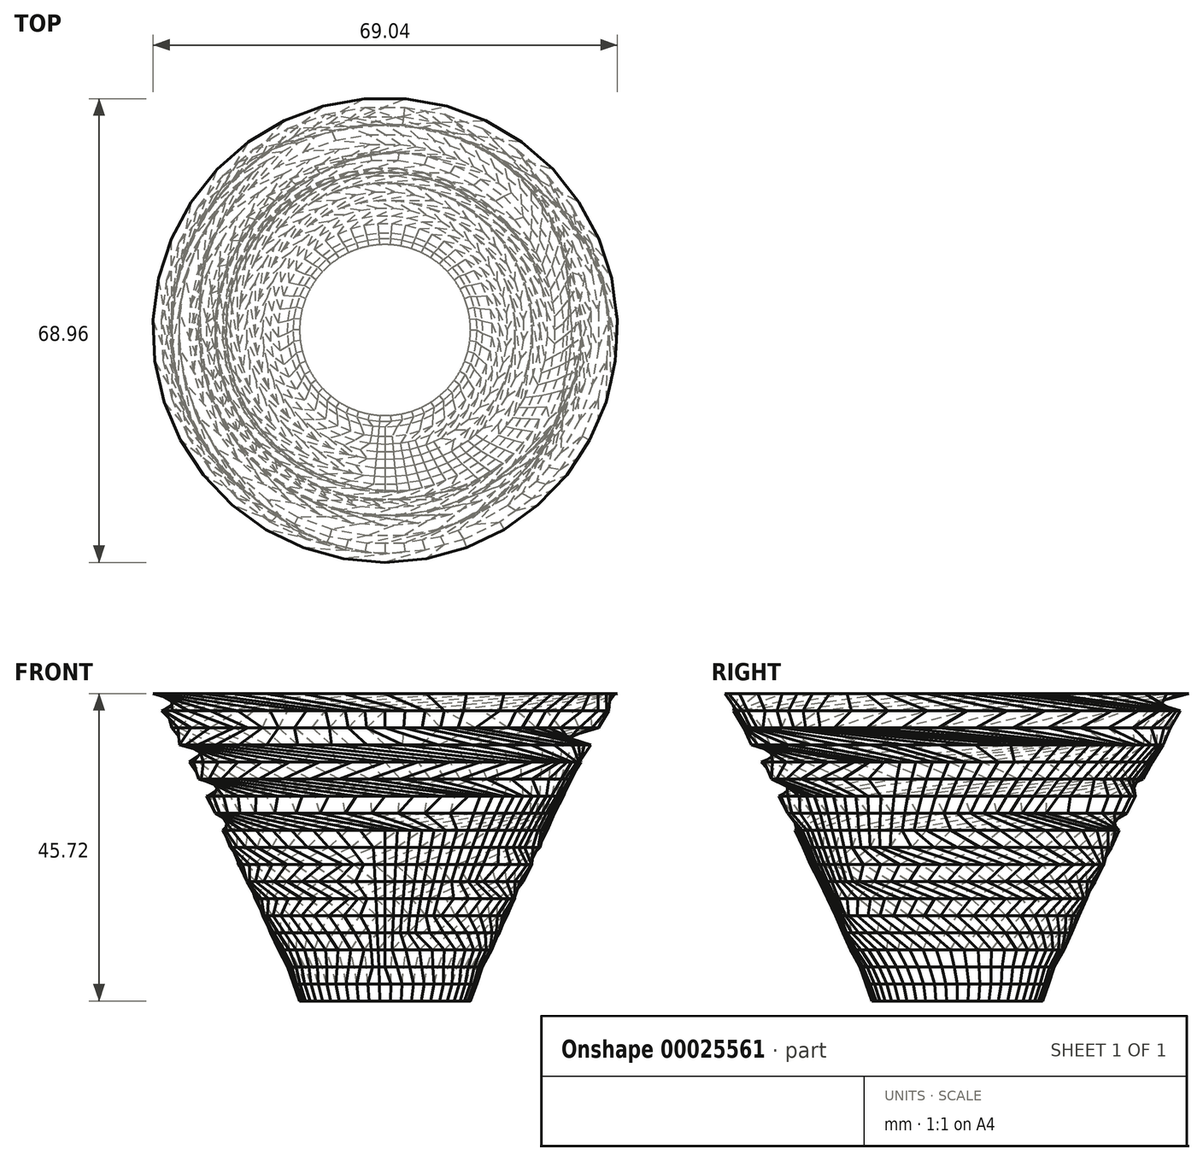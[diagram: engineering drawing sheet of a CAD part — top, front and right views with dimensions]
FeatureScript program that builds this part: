
annotation { "Feature Type Name" : "Feature", "Feature Type Description" : "" }
export const myFeature = defineFeature(function(context is Context, id is Id, definition is map)
    precondition{}
    {
        {
            var Q0;
            Q0=qCreatedBy(makeId("Top.planeOp"),FACE);
            var sketch = newSketch(context, id + "F0", { "sketchPlane" : qUnion([Q0])});
            skCircle(sketch, "E0", {"center": v(0, 0) * mm, "radius": 12.7 * mm});
            skSolve(sketch);
        }
        {
            var Q0;
            Q0=qCreatedBy(makeId("Top.planeOp"),FACE);
            cPlane(context, id + "F1", {"entities" : qUnion([Q0]), "cplaneType" : CPlaneType.OFFSET, "offset" : 2.54 * mm, "width" : 152.4 * mm, "height" : 152.4 * mm});
        }
        {
            var Q0;
            Q0=qCreatedBy(id+"F1.planeOp",FACE);
            var sketch = newSketch(context, id + "F2", { "sketchPlane" : qUnion([Q0])});
            skPoint(sketch, "E1.0", {"position": v(0, 0) * mm});
            skCircle(sketch, "E2.cCircle", {"center": v(0, 0) * mm, "radius": 13.6 * mm, "construction": true});
            skLineSegment(sketch, "E2.0", {"start": v(-0.86, 13.6) * mm, "end": v(0.86, 13.6) * mm});
            skLineSegment(sketch, "E2.1", {"start": v(0.86, 13.6) * mm, "end": v(2.55, 13.38) * mm});
            skLineSegment(sketch, "E2.2", {"start": v(2.55, 13.38) * mm, "end": v(4.2, 12.95) * mm});
            skLineSegment(sketch, "E2.3", {"start": v(4.2, 12.95) * mm, "end": v(5.8, 12.33) * mm});
            skLineSegment(sketch, "E2.4", {"start": v(5.8, 12.33) * mm, "end": v(7.3, 11.5) * mm});
            skLineSegment(sketch, "E2.5", {"start": v(7.3, 11.5) * mm, "end": v(8.68, 10.5) * mm});
            skLineSegment(sketch, "E2.6", {"start": v(8.68, 10.5) * mm, "end": v(9.93, 9.32) * mm});
            skLineSegment(sketch, "E2.7", {"start": v(9.93, 9.32) * mm, "end": v(11.02, 8) * mm});
            skLineSegment(sketch, "E2.8", {"start": v(11.02, 8) * mm, "end": v(11.94, 6.56) * mm});
            skLineSegment(sketch, "E2.9", {"start": v(11.94, 6.56) * mm, "end": v(12.66, 5.01) * mm});
            skLineSegment(sketch, "E2.10", {"start": v(12.66, 5.01) * mm, "end": v(13.2, 3.39) * mm});
            skLineSegment(sketch, "E2.11", {"start": v(13.2, 3.39) * mm, "end": v(13.51, 1.7) * mm});
            skLineSegment(sketch, "E2.12", {"start": v(13.51, 1.7) * mm, "end": v(13.62, 0) * mm});
            skLineSegment(sketch, "E2.13", {"start": v(13.62, 0) * mm, "end": v(13.51, -1.7) * mm});
            skLineSegment(sketch, "E2.14", {"start": v(13.51, -1.7) * mm, "end": v(13.2, -3.39) * mm});
            skLineSegment(sketch, "E2.15", {"start": v(13.2, -3.39) * mm, "end": v(12.66, -5.01) * mm});
            skLineSegment(sketch, "E2.16", {"start": v(12.66, -5.01) * mm, "end": v(11.94, -6.56) * mm});
            skLineSegment(sketch, "E2.17", {"start": v(11.94, -6.56) * mm, "end": v(11.02, -8) * mm});
            skLineSegment(sketch, "E2.18", {"start": v(11.02, -8) * mm, "end": v(9.93, -9.32) * mm});
            skLineSegment(sketch, "E2.19", {"start": v(9.93, -9.32) * mm, "end": v(8.68, -10.5) * mm});
            skLineSegment(sketch, "E2.20", {"start": v(8.68, -10.5) * mm, "end": v(7.3, -11.5) * mm});
            skLineSegment(sketch, "E2.21", {"start": v(7.3, -11.5) * mm, "end": v(5.8, -12.33) * mm});
            skLineSegment(sketch, "E2.22", {"start": v(5.8, -12.33) * mm, "end": v(4.2, -12.95) * mm});
            skLineSegment(sketch, "E2.23", {"start": v(4.2, -12.95) * mm, "end": v(2.55, -13.38) * mm});
            skLineSegment(sketch, "E2.24", {"start": v(2.55, -13.38) * mm, "end": v(0.86, -13.6) * mm});
            skLineSegment(sketch, "E2.25", {"start": v(0.86, -13.6) * mm, "end": v(-0.86, -13.6) * mm});
            skLineSegment(sketch, "E2.26", {"start": v(-0.86, -13.6) * mm, "end": v(-2.55, -13.38) * mm});
            skLineSegment(sketch, "E2.27", {"start": v(-2.55, -13.38) * mm, "end": v(-4.2, -12.95) * mm});
            skLineSegment(sketch, "E2.28", {"start": v(-4.2, -12.95) * mm, "end": v(-5.8, -12.33) * mm});
            skLineSegment(sketch, "E2.29", {"start": v(-5.8, -12.33) * mm, "end": v(-7.3, -11.5) * mm});
            skLineSegment(sketch, "E2.30", {"start": v(-7.3, -11.5) * mm, "end": v(-8.68, -10.5) * mm});
            skLineSegment(sketch, "E2.31", {"start": v(-8.68, -10.5) * mm, "end": v(-9.93, -9.32) * mm});
            skLineSegment(sketch, "E2.32", {"start": v(-9.93, -9.32) * mm, "end": v(-11.02, -8) * mm});
            skLineSegment(sketch, "E2.33", {"start": v(-11.02, -8) * mm, "end": v(-11.94, -6.56) * mm});
            skLineSegment(sketch, "E2.34", {"start": v(-11.94, -6.56) * mm, "end": v(-12.66, -5.01) * mm});
            skLineSegment(sketch, "E2.35", {"start": v(-12.66, -5.01) * mm, "end": v(-13.2, -3.39) * mm});
            skLineSegment(sketch, "E2.36", {"start": v(-13.2, -3.39) * mm, "end": v(-13.51, -1.7) * mm});
            skLineSegment(sketch, "E2.37", {"start": v(-13.51, -1.7) * mm, "end": v(-13.62, 0) * mm});
            skLineSegment(sketch, "E2.38", {"start": v(-13.62, 0) * mm, "end": v(-13.51, 1.7) * mm});
            skLineSegment(sketch, "E2.39", {"start": v(-13.51, 1.7) * mm, "end": v(-13.2, 3.39) * mm});
            skLineSegment(sketch, "E2.40", {"start": v(-13.2, 3.39) * mm, "end": v(-12.66, 5.01) * mm});
            skLineSegment(sketch, "E2.41", {"start": v(-12.66, 5.01) * mm, "end": v(-11.94, 6.56) * mm});
            skLineSegment(sketch, "E2.42", {"start": v(-11.94, 6.56) * mm, "end": v(-11.02, 8) * mm});
            skLineSegment(sketch, "E2.43", {"start": v(-11.02, 8) * mm, "end": v(-9.93, 9.32) * mm});
            skLineSegment(sketch, "E2.44", {"start": v(-9.93, 9.32) * mm, "end": v(-8.68, 10.5) * mm});
            skLineSegment(sketch, "E2.45", {"start": v(-8.68, 10.5) * mm, "end": v(-7.3, 11.5) * mm});
            skLineSegment(sketch, "E2.46", {"start": v(-7.3, 11.5) * mm, "end": v(-5.8, 12.33) * mm});
            skLineSegment(sketch, "E2.47", {"start": v(-5.8, 12.33) * mm, "end": v(-4.2, 12.95) * mm});
            skLineSegment(sketch, "E2.48", {"start": v(-4.2, 12.95) * mm, "end": v(-2.55, 13.38) * mm});
            skLineSegment(sketch, "E2.49", {"start": v(-2.55, 13.38) * mm, "end": v(-0.86, 13.6) * mm});
            skPoint(sketch, "E2.0.midPoint", {"position": v(0, 13.6) * mm});
            skSolve(sketch);
        }
        {
            var Q0;
            Q0=makeQuery(id+"F0.imprint","IMPRINT",FACE,{"disambiguationData":[TD([[makeQuery(id+"F0.imprint","IMPRINT",EDGE,{"derivedFrom":sQuery(id+"F0.wireOp",EDGE,"E0")}),1.0]])]});
            var Q1;
            Q1=makeQuery(id+"F2.imprint","IMPRINT",FACE,{"disambiguationData":[TD([[makeQuery(id+"F2.imprint","IMPRINT",EDGE,{"derivedFrom":sQuery(id+"F2.wireOp",EDGE,"E2.0")}),-1.0]])]});
            loft(context, id + "F3", {"sheetProfilesArray" : [{ "sheetProfileEntities" : qUnion([Q0]) }, { "sheetProfileEntities" : qUnion([Q1]) }]});
        }
        {
            var Q0;
            Q0=qCreatedBy(id+"F1.planeOp",FACE);
            cPlane(context, id + "F4", {"entities" : qUnion([Q0]), "cplaneType" : CPlaneType.OFFSET, "offset" : 2.54 * mm, "width" : 152.4 * mm, "height" : 152.4 * mm});
        }
        {
            var Q0;
            Q0=qCreatedBy(id+"F4.planeOp",FACE);
            var sketch = newSketch(context, id + "F5", { "sketchPlane" : qUnion([Q0])});
            skCircle(sketch, "E3.cCircle", {"center": v(0, 0) * mm, "radius": 14.44 * mm, "construction": true});
            skLineSegment(sketch, "E3.0", {"start": v(-0.93, 14.44) * mm, "end": v(0.93, 14.44) * mm});
            skLineSegment(sketch, "E3.1", {"start": v(0.93, 14.44) * mm, "end": v(2.77, 14.2) * mm});
            skLineSegment(sketch, "E3.2", {"start": v(2.77, 14.2) * mm, "end": v(4.56, 13.74) * mm});
            skLineSegment(sketch, "E3.3", {"start": v(4.56, 13.74) * mm, "end": v(6.28, 13.04) * mm});
            skLineSegment(sketch, "E3.4", {"start": v(6.28, 13.04) * mm, "end": v(7.9, 12.13) * mm});
            skLineSegment(sketch, "E3.5", {"start": v(7.9, 12.13) * mm, "end": v(9.38, 11.02) * mm});
            skLineSegment(sketch, "E3.6", {"start": v(9.38, 11.02) * mm, "end": v(10.71, 9.73) * mm});
            skLineSegment(sketch, "E3.7", {"start": v(10.71, 9.73) * mm, "end": v(11.87, 8.28) * mm});
            skLineSegment(sketch, "E3.8", {"start": v(11.87, 8.28) * mm, "end": v(12.83, 6.7) * mm});
            skLineSegment(sketch, "E3.9", {"start": v(12.83, 6.7) * mm, "end": v(13.58, 5) * mm});
            skLineSegment(sketch, "E3.10", {"start": v(13.58, 5) * mm, "end": v(14.11, 3.22) * mm});
            skLineSegment(sketch, "E3.11", {"start": v(14.11, 3.22) * mm, "end": v(14.4, 1.39) * mm});
            skLineSegment(sketch, "E3.12", {"start": v(14.4, 1.39) * mm, "end": v(14.47, -0.46) * mm});
            skLineSegment(sketch, "E3.13", {"start": v(14.47, -0.46) * mm, "end": v(14.29, -2.31) * mm});
            skLineSegment(sketch, "E3.14", {"start": v(14.29, -2.31) * mm, "end": v(13.88, -4.12) * mm});
            skLineSegment(sketch, "E3.15", {"start": v(13.88, -4.12) * mm, "end": v(13.24, -5.86) * mm});
            skLineSegment(sketch, "E3.16", {"start": v(13.24, -5.86) * mm, "end": v(12.38, -7.5) * mm});
            skLineSegment(sketch, "E3.17", {"start": v(12.38, -7.5) * mm, "end": v(11.32, -9.02) * mm});
            skLineSegment(sketch, "E3.18", {"start": v(11.32, -9.02) * mm, "end": v(10.07, -10.4) * mm});
            skLineSegment(sketch, "E3.19", {"start": v(10.07, -10.4) * mm, "end": v(8.66, -11.6) * mm});
            skLineSegment(sketch, "E3.20", {"start": v(8.66, -11.6) * mm, "end": v(7.1, -12.61) * mm});
            skLineSegment(sketch, "E3.21", {"start": v(7.1, -12.61) * mm, "end": v(5.43, -13.42) * mm});
            skLineSegment(sketch, "E3.22", {"start": v(5.43, -13.42) * mm, "end": v(3.67, -14) * mm});
            skLineSegment(sketch, "E3.23", {"start": v(3.67, -14) * mm, "end": v(1.85, -14.36) * mm});
            skLineSegment(sketch, "E3.24", {"start": v(1.85, -14.36) * mm, "end": v(0, -14.47) * mm});
            skLineSegment(sketch, "E3.25", {"start": v(0, -14.47) * mm, "end": v(-1.85, -14.36) * mm});
            skLineSegment(sketch, "E3.26", {"start": v(-1.85, -14.36) * mm, "end": v(-3.67, -14) * mm});
            skLineSegment(sketch, "E3.27", {"start": v(-3.67, -14) * mm, "end": v(-5.43, -13.42) * mm});
            skLineSegment(sketch, "E3.28", {"start": v(-5.43, -13.42) * mm, "end": v(-7.1, -12.61) * mm});
            skLineSegment(sketch, "E3.29", {"start": v(-7.1, -12.61) * mm, "end": v(-8.66, -11.6) * mm});
            skLineSegment(sketch, "E3.30", {"start": v(-8.66, -11.6) * mm, "end": v(-10.07, -10.4) * mm});
            skLineSegment(sketch, "E3.31", {"start": v(-10.07, -10.4) * mm, "end": v(-11.32, -9.02) * mm});
            skLineSegment(sketch, "E3.32", {"start": v(-11.32, -9.02) * mm, "end": v(-12.38, -7.5) * mm});
            skLineSegment(sketch, "E3.33", {"start": v(-12.38, -7.5) * mm, "end": v(-13.24, -5.86) * mm});
            skLineSegment(sketch, "E3.34", {"start": v(-13.24, -5.86) * mm, "end": v(-13.88, -4.12) * mm});
            skLineSegment(sketch, "E3.35", {"start": v(-13.88, -4.12) * mm, "end": v(-14.29, -2.31) * mm});
            skLineSegment(sketch, "E3.36", {"start": v(-14.29, -2.31) * mm, "end": v(-14.47, -0.46) * mm});
            skLineSegment(sketch, "E3.37", {"start": v(-14.47, -0.46) * mm, "end": v(-14.4, 1.39) * mm});
            skLineSegment(sketch, "E3.38", {"start": v(-14.4, 1.39) * mm, "end": v(-14.11, 3.22) * mm});
            skLineSegment(sketch, "E3.39", {"start": v(-14.11, 3.22) * mm, "end": v(-13.58, 5) * mm});
            skLineSegment(sketch, "E3.40", {"start": v(-13.58, 5) * mm, "end": v(-12.83, 6.7) * mm});
            skLineSegment(sketch, "E3.41", {"start": v(-12.83, 6.7) * mm, "end": v(-11.87, 8.28) * mm});
            skLineSegment(sketch, "E3.42", {"start": v(-11.87, 8.28) * mm, "end": v(-10.71, 9.73) * mm});
            skLineSegment(sketch, "E3.43", {"start": v(-10.71, 9.73) * mm, "end": v(-9.38, 11.02) * mm});
            skLineSegment(sketch, "E3.44", {"start": v(-9.38, 11.02) * mm, "end": v(-7.9, 12.13) * mm});
            skLineSegment(sketch, "E3.45", {"start": v(-7.9, 12.13) * mm, "end": v(-6.28, 13.04) * mm});
            skLineSegment(sketch, "E3.46", {"start": v(-6.28, 13.04) * mm, "end": v(-4.56, 13.74) * mm});
            skLineSegment(sketch, "E3.47", {"start": v(-4.56, 13.74) * mm, "end": v(-2.77, 14.2) * mm});
            skLineSegment(sketch, "E3.48", {"start": v(-2.77, 14.2) * mm, "end": v(-0.93, 14.44) * mm});
            skPoint(sketch, "E3.0.midPoint", {"position": v(0, 14.44) * mm});
            skSolve(sketch);
        }
        {
            var Q1;
            Q1=makeQuery(id+"F3.opLoft","CAP_FACE",FACE,{"disambiguationData":[OSD([makeQuery(id+"F2.imprint","IMPRINT",FACE,{"disambiguationData":[TD([[makeQuery(id+"F2.imprint","IMPRINT",EDGE,{"derivedFrom":sQuery(id+"F2.wireOp",EDGE,"E2.0")}),-1.0]])]})])],"isStart":true});
            var Q2;
            Q2=makeQuery(id+"F5.imprint","IMPRINT",FACE,{"disambiguationData":[TD([[makeQuery(id+"F5.imprint","IMPRINT",EDGE,{"derivedFrom":sQuery(id+"F5.wireOp",EDGE,"E3.0")}),-1.0]])]});
            loft(context, id + "F6", {"operationType" : NewBodyOperationType.ADD, "sheetProfilesArray" : [{ "sheetProfileEntities" : qUnion([Q1]) }, { "sheetProfileEntities" : qUnion([Q2]) }]});
        }
        {
            var Q0;
            Q0=qCreatedBy(id+"F4.planeOp",FACE);
            cPlane(context, id + "F7", {"entities" : qUnion([Q0]), "cplaneType" : CPlaneType.OFFSET, "offset" : 2.54 * mm, "width" : 152.4 * mm, "height" : 152.4 * mm});
        }
        {
            var Q0;
            Q0=qCreatedBy(id+"F7.planeOp",FACE);
            var sketch = newSketch(context, id + "F8", { "sketchPlane" : qUnion([Q0])});
            skCircle(sketch, "E4.cCircle", {"center": v(0, 0) * mm, "radius": 15.86 * mm, "construction": true});
            skLineSegment(sketch, "E4.0", {"start": v(-1.04, 15.86) * mm, "end": v(1.04, 15.86) * mm});
            skLineSegment(sketch, "E4.1", {"start": v(1.04, 15.86) * mm, "end": v(3.1, 15.59) * mm});
            skLineSegment(sketch, "E4.2", {"start": v(3.1, 15.59) * mm, "end": v(5.1, 15.05) * mm});
            skLineSegment(sketch, "E4.3", {"start": v(5.1, 15.05) * mm, "end": v(7.03, 14.26) * mm});
            skLineSegment(sketch, "E4.4", {"start": v(7.03, 14.26) * mm, "end": v(8.83, 13.22) * mm});
            skLineSegment(sketch, "E4.5", {"start": v(8.83, 13.22) * mm, "end": v(10.48, 11.95) * mm});
            skLineSegment(sketch, "E4.6", {"start": v(10.48, 11.95) * mm, "end": v(11.95, 10.48) * mm});
            skLineSegment(sketch, "E4.7", {"start": v(11.95, 10.48) * mm, "end": v(13.22, 8.83) * mm});
            skLineSegment(sketch, "E4.8", {"start": v(13.22, 8.83) * mm, "end": v(14.26, 7.03) * mm});
            skLineSegment(sketch, "E4.9", {"start": v(14.26, 7.03) * mm, "end": v(15.05, 5.1) * mm});
            skLineSegment(sketch, "E4.10", {"start": v(15.05, 5.1) * mm, "end": v(15.59, 3.1) * mm});
            skLineSegment(sketch, "E4.11", {"start": v(15.59, 3.1) * mm, "end": v(15.86, 1.04) * mm});
            skLineSegment(sketch, "E4.12", {"start": v(15.86, 1.04) * mm, "end": v(15.86, -1.04) * mm});
            skLineSegment(sketch, "E4.13", {"start": v(15.86, -1.04) * mm, "end": v(15.59, -3.1) * mm});
            skLineSegment(sketch, "E4.14", {"start": v(15.59, -3.1) * mm, "end": v(15.05, -5.1) * mm});
            skLineSegment(sketch, "E4.15", {"start": v(15.05, -5.1) * mm, "end": v(14.26, -7.03) * mm});
            skLineSegment(sketch, "E4.16", {"start": v(14.26, -7.03) * mm, "end": v(13.22, -8.83) * mm});
            skLineSegment(sketch, "E4.17", {"start": v(13.22, -8.83) * mm, "end": v(11.95, -10.48) * mm});
            skLineSegment(sketch, "E4.18", {"start": v(11.95, -10.48) * mm, "end": v(10.48, -11.95) * mm});
            skLineSegment(sketch, "E4.19", {"start": v(10.48, -11.95) * mm, "end": v(8.83, -13.22) * mm});
            skLineSegment(sketch, "E4.20", {"start": v(8.83, -13.22) * mm, "end": v(7.03, -14.26) * mm});
            skLineSegment(sketch, "E4.21", {"start": v(7.03, -14.26) * mm, "end": v(5.1, -15.05) * mm});
            skLineSegment(sketch, "E4.22", {"start": v(5.1, -15.05) * mm, "end": v(3.1, -15.59) * mm});
            skLineSegment(sketch, "E4.23", {"start": v(3.1, -15.59) * mm, "end": v(1.04, -15.86) * mm});
            skLineSegment(sketch, "E4.24", {"start": v(1.04, -15.86) * mm, "end": v(-1.04, -15.86) * mm});
            skLineSegment(sketch, "E4.25", {"start": v(-1.04, -15.86) * mm, "end": v(-3.1, -15.59) * mm});
            skLineSegment(sketch, "E4.26", {"start": v(-3.1, -15.59) * mm, "end": v(-5.1, -15.05) * mm});
            skLineSegment(sketch, "E4.27", {"start": v(-5.1, -15.05) * mm, "end": v(-7.03, -14.26) * mm});
            skLineSegment(sketch, "E4.28", {"start": v(-7.03, -14.26) * mm, "end": v(-8.83, -13.22) * mm});
            skLineSegment(sketch, "E4.29", {"start": v(-8.83, -13.22) * mm, "end": v(-10.48, -11.95) * mm});
            skLineSegment(sketch, "E4.30", {"start": v(-10.48, -11.95) * mm, "end": v(-11.95, -10.48) * mm});
            skLineSegment(sketch, "E4.31", {"start": v(-11.95, -10.48) * mm, "end": v(-13.22, -8.83) * mm});
            skLineSegment(sketch, "E4.32", {"start": v(-13.22, -8.83) * mm, "end": v(-14.26, -7.03) * mm});
            skLineSegment(sketch, "E4.33", {"start": v(-14.26, -7.03) * mm, "end": v(-15.05, -5.1) * mm});
            skLineSegment(sketch, "E4.34", {"start": v(-15.05, -5.1) * mm, "end": v(-15.59, -3.1) * mm});
            skLineSegment(sketch, "E4.35", {"start": v(-15.59, -3.1) * mm, "end": v(-15.86, -1.04) * mm});
            skLineSegment(sketch, "E4.36", {"start": v(-15.86, -1.04) * mm, "end": v(-15.86, 1.04) * mm});
            skLineSegment(sketch, "E4.37", {"start": v(-15.86, 1.04) * mm, "end": v(-15.59, 3.1) * mm});
            skLineSegment(sketch, "E4.38", {"start": v(-15.59, 3.1) * mm, "end": v(-15.05, 5.1) * mm});
            skLineSegment(sketch, "E4.39", {"start": v(-15.05, 5.1) * mm, "end": v(-14.26, 7.03) * mm});
            skLineSegment(sketch, "E4.40", {"start": v(-14.26, 7.03) * mm, "end": v(-13.22, 8.83) * mm});
            skLineSegment(sketch, "E4.41", {"start": v(-13.22, 8.83) * mm, "end": v(-11.95, 10.48) * mm});
            skLineSegment(sketch, "E4.42", {"start": v(-11.95, 10.48) * mm, "end": v(-10.48, 11.95) * mm});
            skLineSegment(sketch, "E4.43", {"start": v(-10.48, 11.95) * mm, "end": v(-8.83, 13.22) * mm});
            skLineSegment(sketch, "E4.44", {"start": v(-8.83, 13.22) * mm, "end": v(-7.03, 14.26) * mm});
            skLineSegment(sketch, "E4.45", {"start": v(-7.03, 14.26) * mm, "end": v(-5.1, 15.05) * mm});
            skLineSegment(sketch, "E4.46", {"start": v(-5.1, 15.05) * mm, "end": v(-3.1, 15.59) * mm});
            skLineSegment(sketch, "E4.47", {"start": v(-3.1, 15.59) * mm, "end": v(-1.04, 15.86) * mm});
            skPoint(sketch, "E4.0.midPoint", {"position": v(0, 15.86) * mm});
            skSolve(sketch);
        }
        {
            var Q1;
            Q1=makeQuery(id+"F6.opLoft","CAP_FACE",FACE,{"disambiguationData":[OSD([makeQuery(id+"F5.imprint","IMPRINT",FACE,{"disambiguationData":[TD([[makeQuery(id+"F5.imprint","IMPRINT",EDGE,{"derivedFrom":sQuery(id+"F5.wireOp",EDGE,"E3.0")}),-1.0]])]})])],"isStart":true});
            var Q2;
            Q2=makeQuery(id+"F8.imprint","IMPRINT",FACE,{"disambiguationData":[TD([[makeQuery(id+"F8.imprint","IMPRINT",EDGE,{"derivedFrom":sQuery(id+"F8.wireOp",EDGE,"E4.0")}),-1.0]])]});
            loft(context, id + "F9", {"operationType" : NewBodyOperationType.ADD, "sheetProfilesArray" : [{ "sheetProfileEntities" : qUnion([Q1]) }, { "sheetProfileEntities" : qUnion([Q2]) }]});
        }
        {
            var Q0;
            Q0=qCreatedBy(id+"F7.planeOp",FACE);
            cPlane(context, id + "F10", {"entities" : qUnion([Q0]), "cplaneType" : CPlaneType.OFFSET, "offset" : 2.54 * mm, "width" : 152.4 * mm, "height" : 152.4 * mm});
        }
        {
            var Q0;
            Q0=qCreatedBy(id+"F10.planeOp",FACE);
            var sketch = newSketch(context, id + "F11", { "sketchPlane" : qUnion([Q0])});
            skCircle(sketch, "E5.cCircle", {"center": v(0, 0) * mm, "radius": 17 * mm, "construction": true});
            skLineSegment(sketch, "E5.0", {"start": v(-1.14, 17) * mm, "end": v(1.14, 17) * mm});
            skLineSegment(sketch, "E5.1", {"start": v(1.14, 17) * mm, "end": v(3.4, 16.7) * mm});
            skLineSegment(sketch, "E5.2", {"start": v(3.4, 16.7) * mm, "end": v(5.59, 16.09) * mm});
            skLineSegment(sketch, "E5.3", {"start": v(5.59, 16.09) * mm, "end": v(7.68, 15.2) * mm});
            skLineSegment(sketch, "E5.4", {"start": v(7.68, 15.2) * mm, "end": v(9.64, 14.04) * mm});
            skLineSegment(sketch, "E5.5", {"start": v(9.64, 14.04) * mm, "end": v(11.42, 12.63) * mm});
            skLineSegment(sketch, "E5.6", {"start": v(11.42, 12.63) * mm, "end": v(13, 11) * mm});
            skLineSegment(sketch, "E5.7", {"start": v(13, 11) * mm, "end": v(14.36, 9.16) * mm});
            skLineSegment(sketch, "E5.8", {"start": v(14.36, 9.16) * mm, "end": v(15.45, 7.17) * mm});
            skLineSegment(sketch, "E5.9", {"start": v(15.45, 7.17) * mm, "end": v(16.27, 5.05) * mm});
            skLineSegment(sketch, "E5.10", {"start": v(16.27, 5.05) * mm, "end": v(16.8, 2.83) * mm});
            skLineSegment(sketch, "E5.11", {"start": v(16.8, 2.83) * mm, "end": v(17.02, 0.57) * mm});
            skLineSegment(sketch, "E5.12", {"start": v(17.02, 0.57) * mm, "end": v(16.95, -1.7) * mm});
            skLineSegment(sketch, "E5.13", {"start": v(16.95, -1.7) * mm, "end": v(16.57, -3.95) * mm});
            skLineSegment(sketch, "E5.14", {"start": v(16.57, -3.95) * mm, "end": v(15.9, -6.12) * mm});
            skLineSegment(sketch, "E5.15", {"start": v(15.9, -6.12) * mm, "end": v(14.94, -8.18) * mm});
            skLineSegment(sketch, "E5.16", {"start": v(14.94, -8.18) * mm, "end": v(13.71, -10.1) * mm});
            skLineSegment(sketch, "E5.17", {"start": v(13.71, -10.1) * mm, "end": v(12.24, -11.84) * mm});
            skLineSegment(sketch, "E5.18", {"start": v(12.24, -11.84) * mm, "end": v(10.56, -13.37) * mm});
            skLineSegment(sketch, "E5.19", {"start": v(10.56, -13.37) * mm, "end": v(8.68, -14.65) * mm});
            skLineSegment(sketch, "E5.20", {"start": v(8.68, -14.65) * mm, "end": v(6.65, -15.68) * mm});
            skLineSegment(sketch, "E5.21", {"start": v(6.65, -15.68) * mm, "end": v(4.5, -16.43) * mm});
            skLineSegment(sketch, "E5.22", {"start": v(4.5, -16.43) * mm, "end": v(2.27, -16.88) * mm});
            skLineSegment(sketch, "E5.23", {"start": v(2.27, -16.88) * mm, "end": v(0, -17.03) * mm});
            skLineSegment(sketch, "E5.24", {"start": v(0, -17.03) * mm, "end": v(-2.27, -16.88) * mm});
            skLineSegment(sketch, "E5.25", {"start": v(-2.27, -16.88) * mm, "end": v(-4.5, -16.43) * mm});
            skLineSegment(sketch, "E5.26", {"start": v(-4.5, -16.43) * mm, "end": v(-6.65, -15.68) * mm});
            skLineSegment(sketch, "E5.27", {"start": v(-6.65, -15.68) * mm, "end": v(-8.68, -14.65) * mm});
            skLineSegment(sketch, "E5.28", {"start": v(-8.68, -14.65) * mm, "end": v(-10.56, -13.37) * mm});
            skLineSegment(sketch, "E5.29", {"start": v(-10.56, -13.37) * mm, "end": v(-12.24, -11.84) * mm});
            skLineSegment(sketch, "E5.30", {"start": v(-12.24, -11.84) * mm, "end": v(-13.71, -10.1) * mm});
            skLineSegment(sketch, "E5.31", {"start": v(-13.71, -10.1) * mm, "end": v(-14.94, -8.18) * mm});
            skLineSegment(sketch, "E5.32", {"start": v(-14.94, -8.18) * mm, "end": v(-15.9, -6.12) * mm});
            skLineSegment(sketch, "E5.33", {"start": v(-15.9, -6.12) * mm, "end": v(-16.57, -3.95) * mm});
            skLineSegment(sketch, "E5.34", {"start": v(-16.57, -3.95) * mm, "end": v(-16.95, -1.7) * mm});
            skLineSegment(sketch, "E5.35", {"start": v(-16.95, -1.7) * mm, "end": v(-17.02, 0.57) * mm});
            skLineSegment(sketch, "E5.36", {"start": v(-17.02, 0.57) * mm, "end": v(-16.8, 2.83) * mm});
            skLineSegment(sketch, "E5.37", {"start": v(-16.8, 2.83) * mm, "end": v(-16.27, 5.05) * mm});
            skLineSegment(sketch, "E5.38", {"start": v(-16.27, 5.05) * mm, "end": v(-15.45, 7.17) * mm});
            skLineSegment(sketch, "E5.39", {"start": v(-15.45, 7.17) * mm, "end": v(-14.36, 9.16) * mm});
            skLineSegment(sketch, "E5.40", {"start": v(-14.36, 9.16) * mm, "end": v(-13, 11) * mm});
            skLineSegment(sketch, "E5.41", {"start": v(-13, 11) * mm, "end": v(-11.42, 12.63) * mm});
            skLineSegment(sketch, "E5.42", {"start": v(-11.42, 12.63) * mm, "end": v(-9.64, 14.04) * mm});
            skLineSegment(sketch, "E5.43", {"start": v(-9.64, 14.04) * mm, "end": v(-7.68, 15.2) * mm});
            skLineSegment(sketch, "E5.44", {"start": v(-7.68, 15.2) * mm, "end": v(-5.59, 16.09) * mm});
            skLineSegment(sketch, "E5.45", {"start": v(-5.59, 16.09) * mm, "end": v(-3.4, 16.7) * mm});
            skLineSegment(sketch, "E5.46", {"start": v(-3.4, 16.7) * mm, "end": v(-1.14, 17) * mm});
            skPoint(sketch, "E5.0.midPoint", {"position": v(0, 17) * mm});
            skSolve(sketch);
        }
        {
            var Q1;
            Q1=makeQuery(id+"F9.opLoft","CAP_FACE",FACE,{"disambiguationData":[OSD([makeQuery(id+"F8.imprint","IMPRINT",FACE,{"disambiguationData":[TD([[makeQuery(id+"F8.imprint","IMPRINT",EDGE,{"derivedFrom":sQuery(id+"F8.wireOp",EDGE,"E4.0")}),-1.0]])]})])],"isStart":true});
            var Q2;
            Q2=makeQuery(id+"F11.imprint","IMPRINT",FACE,{"disambiguationData":[TD([[makeQuery(id+"F11.imprint","IMPRINT",EDGE,{"derivedFrom":sQuery(id+"F11.wireOp",EDGE,"E5.0")}),-1.0]])]});
            loft(context, id + "F12", {"operationType" : NewBodyOperationType.ADD, "sheetProfilesArray" : [{ "sheetProfileEntities" : qUnion([Q1]) }, { "sheetProfileEntities" : qUnion([Q2]) }]});
        }
        {
            var Q0;
            Q0=qCreatedBy(id+"F10.planeOp",FACE);
            cPlane(context, id + "F13", {"entities" : qUnion([Q0]), "cplaneType" : CPlaneType.OFFSET, "offset" : 2.54 * mm, "width" : 152.4 * mm, "height" : 152.4 * mm});
        }
        {
            var Q0;
            Q0=qCreatedBy(id+"F13.planeOp",FACE);
            var sketch = newSketch(context, id + "F14", { "sketchPlane" : qUnion([Q0])});
            skCircle(sketch, "E6.cCircle", {"center": v(0, 0) * mm, "radius": 18.13 * mm, "construction": true});
            skLineSegment(sketch, "E6.0", {"start": v(-1.24, 18.13) * mm, "end": v(1.24, 18.13) * mm});
            skLineSegment(sketch, "E6.1", {"start": v(1.24, 18.13) * mm, "end": v(3.7, 17.79) * mm});
            skLineSegment(sketch, "E6.2", {"start": v(3.7, 17.79) * mm, "end": v(6.08, 17.12) * mm});
            skLineSegment(sketch, "E6.3", {"start": v(6.08, 17.12) * mm, "end": v(8.36, 16.13) * mm});
            skLineSegment(sketch, "E6.4", {"start": v(8.36, 16.13) * mm, "end": v(10.48, 14.84) * mm});
            skLineSegment(sketch, "E6.5", {"start": v(10.48, 14.84) * mm, "end": v(12.4, 13.28) * mm});
            skLineSegment(sketch, "E6.6", {"start": v(12.4, 13.28) * mm, "end": v(14.1, 11.47) * mm});
            skLineSegment(sketch, "E6.7", {"start": v(14.1, 11.47) * mm, "end": v(15.52, 9.44) * mm});
            skLineSegment(sketch, "E6.8", {"start": v(15.52, 9.44) * mm, "end": v(16.66, 7.24) * mm});
            skLineSegment(sketch, "E6.9", {"start": v(16.66, 7.24) * mm, "end": v(17.5, 4.9) * mm});
            skLineSegment(sketch, "E6.10", {"start": v(17.5, 4.9) * mm, "end": v(18, 2.47) * mm});
            skLineSegment(sketch, "E6.11", {"start": v(18, 2.47) * mm, "end": v(18.17, 0) * mm});
            skLineSegment(sketch, "E6.12", {"start": v(18.17, 0) * mm, "end": v(18, -2.47) * mm});
            skLineSegment(sketch, "E6.13", {"start": v(18, -2.47) * mm, "end": v(17.5, -4.9) * mm});
            skLineSegment(sketch, "E6.14", {"start": v(17.5, -4.9) * mm, "end": v(16.66, -7.24) * mm});
            skLineSegment(sketch, "E6.15", {"start": v(16.66, -7.24) * mm, "end": v(15.52, -9.44) * mm});
            skLineSegment(sketch, "E6.16", {"start": v(15.52, -9.44) * mm, "end": v(14.1, -11.47) * mm});
            skLineSegment(sketch, "E6.17", {"start": v(14.1, -11.47) * mm, "end": v(12.4, -13.28) * mm});
            skLineSegment(sketch, "E6.18", {"start": v(12.4, -13.28) * mm, "end": v(10.48, -14.84) * mm});
            skLineSegment(sketch, "E6.19", {"start": v(10.48, -14.84) * mm, "end": v(8.36, -16.13) * mm});
            skLineSegment(sketch, "E6.20", {"start": v(8.36, -16.13) * mm, "end": v(6.08, -17.12) * mm});
            skLineSegment(sketch, "E6.21", {"start": v(6.08, -17.12) * mm, "end": v(3.7, -17.79) * mm});
            skLineSegment(sketch, "E6.22", {"start": v(3.7, -17.79) * mm, "end": v(1.24, -18.13) * mm});
            skLineSegment(sketch, "E6.23", {"start": v(1.24, -18.13) * mm, "end": v(-1.24, -18.13) * mm});
            skLineSegment(sketch, "E6.24", {"start": v(-1.24, -18.13) * mm, "end": v(-3.7, -17.79) * mm});
            skLineSegment(sketch, "E6.25", {"start": v(-3.7, -17.79) * mm, "end": v(-6.08, -17.12) * mm});
            skLineSegment(sketch, "E6.26", {"start": v(-6.08, -17.12) * mm, "end": v(-8.36, -16.13) * mm});
            skLineSegment(sketch, "E6.27", {"start": v(-8.36, -16.13) * mm, "end": v(-10.48, -14.84) * mm});
            skLineSegment(sketch, "E6.28", {"start": v(-10.48, -14.84) * mm, "end": v(-12.4, -13.28) * mm});
            skLineSegment(sketch, "E6.29", {"start": v(-12.4, -13.28) * mm, "end": v(-14.1, -11.47) * mm});
            skLineSegment(sketch, "E6.30", {"start": v(-14.1, -11.47) * mm, "end": v(-15.52, -9.44) * mm});
            skLineSegment(sketch, "E6.31", {"start": v(-15.52, -9.44) * mm, "end": v(-16.66, -7.24) * mm});
            skLineSegment(sketch, "E6.32", {"start": v(-16.66, -7.24) * mm, "end": v(-17.5, -4.9) * mm});
            skLineSegment(sketch, "E6.33", {"start": v(-17.5, -4.9) * mm, "end": v(-18, -2.47) * mm});
            skLineSegment(sketch, "E6.34", {"start": v(-18, -2.47) * mm, "end": v(-18.17, 0) * mm});
            skLineSegment(sketch, "E6.35", {"start": v(-18.17, 0) * mm, "end": v(-18, 2.47) * mm});
            skLineSegment(sketch, "E6.36", {"start": v(-18, 2.47) * mm, "end": v(-17.5, 4.9) * mm});
            skLineSegment(sketch, "E6.37", {"start": v(-17.5, 4.9) * mm, "end": v(-16.66, 7.24) * mm});
            skLineSegment(sketch, "E6.38", {"start": v(-16.66, 7.24) * mm, "end": v(-15.52, 9.44) * mm});
            skLineSegment(sketch, "E6.39", {"start": v(-15.52, 9.44) * mm, "end": v(-14.1, 11.47) * mm});
            skLineSegment(sketch, "E6.40", {"start": v(-14.1, 11.47) * mm, "end": v(-12.4, 13.28) * mm});
            skLineSegment(sketch, "E6.41", {"start": v(-12.4, 13.28) * mm, "end": v(-10.48, 14.84) * mm});
            skLineSegment(sketch, "E6.42", {"start": v(-10.48, 14.84) * mm, "end": v(-8.36, 16.13) * mm});
            skLineSegment(sketch, "E6.43", {"start": v(-8.36, 16.13) * mm, "end": v(-6.08, 17.12) * mm});
            skLineSegment(sketch, "E6.44", {"start": v(-6.08, 17.12) * mm, "end": v(-3.7, 17.79) * mm});
            skLineSegment(sketch, "E6.45", {"start": v(-3.7, 17.79) * mm, "end": v(-1.24, 18.13) * mm});
            skPoint(sketch, "E6.0.midPoint", {"position": v(0, 18.13) * mm});
            skSolve(sketch);
        }
        {
            var Q1;
            Q1=makeQuery(id+"F12.opLoft","CAP_FACE",FACE,{"disambiguationData":[OSD([makeQuery(id+"F11.imprint","IMPRINT",FACE,{"disambiguationData":[TD([[makeQuery(id+"F11.imprint","IMPRINT",EDGE,{"derivedFrom":sQuery(id+"F11.wireOp",EDGE,"E5.0")}),-1.0]])]})])],"isStart":true});
            var Q2;
            Q2=makeQuery(id+"F14.imprint","IMPRINT",FACE,{"disambiguationData":[TD([[makeQuery(id+"F14.imprint","IMPRINT",EDGE,{"derivedFrom":sQuery(id+"F14.wireOp",EDGE,"E6.0")}),-1.0]])]});
            loft(context, id + "F15", {"operationType" : NewBodyOperationType.ADD, "sheetProfilesArray" : [{ "sheetProfileEntities" : qUnion([Q1]) }, { "sheetProfileEntities" : qUnion([Q2]) }]});
        }
        {
            var Q0;
            Q0=qCreatedBy(id+"F13.planeOp",FACE);
            cPlane(context, id + "F16", {"entities" : qUnion([Q0]), "cplaneType" : CPlaneType.OFFSET, "offset" : 2.54 * mm, "width" : 152.4 * mm, "height" : 152.4 * mm});
        }
        {
            var Q0;
            Q0=qCreatedBy(id+"F16.planeOp",FACE);
            var sketch = newSketch(context, id + "F17", { "sketchPlane" : qUnion([Q0])});
            skCircle(sketch, "E7.cCircle", {"center": v(0, 0) * mm, "radius": 19.26 * mm, "construction": true});
            skLineSegment(sketch, "E7.0", {"start": v(-1.35, 19.26) * mm, "end": v(1.35, 19.26) * mm});
            skLineSegment(sketch, "E7.1", {"start": v(1.35, 19.26) * mm, "end": v(4.01, 18.88) * mm});
            skLineSegment(sketch, "E7.2", {"start": v(4.01, 18.88) * mm, "end": v(6.6, 18.14) * mm});
            skLineSegment(sketch, "E7.3", {"start": v(6.6, 18.14) * mm, "end": v(9.06, 17.05) * mm});
            skLineSegment(sketch, "E7.4", {"start": v(9.06, 17.05) * mm, "end": v(11.35, 15.62) * mm});
            skLineSegment(sketch, "E7.5", {"start": v(11.35, 15.62) * mm, "end": v(13.41, 13.89) * mm});
            skLineSegment(sketch, "E7.6", {"start": v(13.41, 13.89) * mm, "end": v(15.21, 11.89) * mm});
            skLineSegment(sketch, "E7.7", {"start": v(15.21, 11.89) * mm, "end": v(16.72, 9.65) * mm});
            skLineSegment(sketch, "E7.8", {"start": v(16.72, 9.65) * mm, "end": v(17.9, 7.23) * mm});
            skLineSegment(sketch, "E7.9", {"start": v(17.9, 7.23) * mm, "end": v(18.73, 4.67) * mm});
            skLineSegment(sketch, "E7.10", {"start": v(18.73, 4.67) * mm, "end": v(19.2, 2.02) * mm});
            skLineSegment(sketch, "E7.11", {"start": v(19.2, 2.02) * mm, "end": v(19.3, -0.67) * mm});
            skLineSegment(sketch, "E7.12", {"start": v(19.3, -0.67) * mm, "end": v(19.01, -3.35) * mm});
            skLineSegment(sketch, "E7.13", {"start": v(19.01, -3.35) * mm, "end": v(18.36, -5.97) * mm});
            skLineSegment(sketch, "E7.14", {"start": v(18.36, -5.97) * mm, "end": v(17.35, -8.46) * mm});
            skLineSegment(sketch, "E7.15", {"start": v(17.35, -8.46) * mm, "end": v(16, -10.8) * mm});
            skLineSegment(sketch, "E7.16", {"start": v(16, -10.8) * mm, "end": v(14.35, -12.92) * mm});
            skLineSegment(sketch, "E7.17", {"start": v(14.35, -12.92) * mm, "end": v(12.4, -14.79) * mm});
            skLineSegment(sketch, "E7.18", {"start": v(12.4, -14.79) * mm, "end": v(10.23, -16.37) * mm});
            skLineSegment(sketch, "E7.19", {"start": v(10.23, -16.37) * mm, "end": v(7.85, -17.64) * mm});
            skLineSegment(sketch, "E7.20", {"start": v(7.85, -17.64) * mm, "end": v(5.32, -18.56) * mm});
            skLineSegment(sketch, "E7.21", {"start": v(5.32, -18.56) * mm, "end": v(2.69, -19.12) * mm});
            skLineSegment(sketch, "E7.22", {"start": v(2.69, -19.12) * mm, "end": v(0, -19.3) * mm});
            skLineSegment(sketch, "E7.23", {"start": v(0, -19.3) * mm, "end": v(-2.69, -19.12) * mm});
            skLineSegment(sketch, "E7.24", {"start": v(-2.69, -19.12) * mm, "end": v(-5.32, -18.56) * mm});
            skLineSegment(sketch, "E7.25", {"start": v(-5.32, -18.56) * mm, "end": v(-7.85, -17.64) * mm});
            skLineSegment(sketch, "E7.26", {"start": v(-7.85, -17.64) * mm, "end": v(-10.23, -16.37) * mm});
            skLineSegment(sketch, "E7.27", {"start": v(-10.23, -16.37) * mm, "end": v(-12.4, -14.79) * mm});
            skLineSegment(sketch, "E7.28", {"start": v(-12.4, -14.79) * mm, "end": v(-14.35, -12.92) * mm});
            skLineSegment(sketch, "E7.29", {"start": v(-14.35, -12.92) * mm, "end": v(-16, -10.8) * mm});
            skLineSegment(sketch, "E7.30", {"start": v(-16, -10.8) * mm, "end": v(-17.35, -8.46) * mm});
            skLineSegment(sketch, "E7.31", {"start": v(-17.35, -8.46) * mm, "end": v(-18.36, -5.97) * mm});
            skLineSegment(sketch, "E7.32", {"start": v(-18.36, -5.97) * mm, "end": v(-19.01, -3.35) * mm});
            skLineSegment(sketch, "E7.33", {"start": v(-19.01, -3.35) * mm, "end": v(-19.3, -0.67) * mm});
            skLineSegment(sketch, "E7.34", {"start": v(-19.3, -0.67) * mm, "end": v(-19.2, 2.02) * mm});
            skLineSegment(sketch, "E7.35", {"start": v(-19.2, 2.02) * mm, "end": v(-18.73, 4.67) * mm});
            skLineSegment(sketch, "E7.36", {"start": v(-18.73, 4.67) * mm, "end": v(-17.9, 7.23) * mm});
            skLineSegment(sketch, "E7.37", {"start": v(-17.9, 7.23) * mm, "end": v(-16.72, 9.65) * mm});
            skLineSegment(sketch, "E7.38", {"start": v(-16.72, 9.65) * mm, "end": v(-15.21, 11.89) * mm});
            skLineSegment(sketch, "E7.39", {"start": v(-15.21, 11.89) * mm, "end": v(-13.41, 13.89) * mm});
            skLineSegment(sketch, "E7.40", {"start": v(-13.41, 13.89) * mm, "end": v(-11.35, 15.62) * mm});
            skLineSegment(sketch, "E7.41", {"start": v(-11.35, 15.62) * mm, "end": v(-9.06, 17.05) * mm});
            skLineSegment(sketch, "E7.42", {"start": v(-9.06, 17.05) * mm, "end": v(-6.6, 18.14) * mm});
            skLineSegment(sketch, "E7.43", {"start": v(-6.6, 18.14) * mm, "end": v(-4.01, 18.88) * mm});
            skLineSegment(sketch, "E7.44", {"start": v(-4.01, 18.88) * mm, "end": v(-1.35, 19.26) * mm});
            skPoint(sketch, "E7.0.midPoint", {"position": v(0, 19.26) * mm});
            skSolve(sketch);
        }
        {
            var Q1;
            Q1=makeQuery(id+"F15.opLoft","CAP_FACE",FACE,{"disambiguationData":[OSD([makeQuery(id+"F14.imprint","IMPRINT",FACE,{"disambiguationData":[TD([[makeQuery(id+"F14.imprint","IMPRINT",EDGE,{"derivedFrom":sQuery(id+"F14.wireOp",EDGE,"E6.0")}),-1.0]])]})])],"isStart":true});
            var Q2;
            Q2=makeQuery(id+"F17.imprint","IMPRINT",FACE,{"disambiguationData":[TD([[makeQuery(id+"F17.imprint","IMPRINT",EDGE,{"derivedFrom":sQuery(id+"F17.wireOp",EDGE,"E7.0")}),-1.0]])]});
            loft(context, id + "F18", {"operationType" : NewBodyOperationType.ADD, "sheetProfilesArray" : [{ "sheetProfileEntities" : qUnion([Q1]) }, { "sheetProfileEntities" : qUnion([Q2]) }]});
        }
        {
            var Q0;
            Q0=qCreatedBy(id+"F16.planeOp",FACE);
            cPlane(context, id + "F19", {"entities" : qUnion([Q0]), "cplaneType" : CPlaneType.OFFSET, "offset" : 2.54 * mm, "width" : 152.4 * mm, "height" : 152.4 * mm});
        }
        {
            var Q0;
            Q0=qCreatedBy(id+"F19.planeOp",FACE);
            var sketch = newSketch(context, id + "F20", { "sketchPlane" : qUnion([Q0])});
            skCircle(sketch, "E8.cCircle", {"center": v(0, 0) * mm, "radius": 20.53 * mm, "construction": true});
            skLineSegment(sketch, "E8.0", {"start": v(-1.47, 20.53) * mm, "end": v(1.47, 20.53) * mm});
            skLineSegment(sketch, "E8.1", {"start": v(1.47, 20.53) * mm, "end": v(4.38, 20.12) * mm});
            skLineSegment(sketch, "E8.2", {"start": v(4.38, 20.12) * mm, "end": v(7.2, 19.29) * mm});
            skLineSegment(sketch, "E8.3", {"start": v(7.2, 19.29) * mm, "end": v(9.87, 18.07) * mm});
            skLineSegment(sketch, "E8.4", {"start": v(9.87, 18.07) * mm, "end": v(12.34, 16.48) * mm});
            skLineSegment(sketch, "E8.5", {"start": v(12.34, 16.48) * mm, "end": v(14.56, 14.56) * mm});
            skLineSegment(sketch, "E8.6", {"start": v(14.56, 14.56) * mm, "end": v(16.48, 12.34) * mm});
            skLineSegment(sketch, "E8.7", {"start": v(16.48, 12.34) * mm, "end": v(18.07, 9.87) * mm});
            skLineSegment(sketch, "E8.8", {"start": v(18.07, 9.87) * mm, "end": v(19.29, 7.2) * mm});
            skLineSegment(sketch, "E8.9", {"start": v(19.29, 7.2) * mm, "end": v(20.12, 4.38) * mm});
            skLineSegment(sketch, "E8.10", {"start": v(20.12, 4.38) * mm, "end": v(20.53, 1.47) * mm});
            skLineSegment(sketch, "E8.11", {"start": v(20.53, 1.47) * mm, "end": v(20.53, -1.47) * mm});
            skLineSegment(sketch, "E8.12", {"start": v(20.53, -1.47) * mm, "end": v(20.12, -4.38) * mm});
            skLineSegment(sketch, "E8.13", {"start": v(20.12, -4.38) * mm, "end": v(19.29, -7.2) * mm});
            skLineSegment(sketch, "E8.14", {"start": v(19.29, -7.2) * mm, "end": v(18.07, -9.87) * mm});
            skLineSegment(sketch, "E8.15", {"start": v(18.07, -9.87) * mm, "end": v(16.48, -12.34) * mm});
            skLineSegment(sketch, "E8.16", {"start": v(16.48, -12.34) * mm, "end": v(14.56, -14.56) * mm});
            skLineSegment(sketch, "E8.17", {"start": v(14.56, -14.56) * mm, "end": v(12.34, -16.48) * mm});
            skLineSegment(sketch, "E8.18", {"start": v(12.34, -16.48) * mm, "end": v(9.87, -18.07) * mm});
            skLineSegment(sketch, "E8.19", {"start": v(9.87, -18.07) * mm, "end": v(7.2, -19.29) * mm});
            skLineSegment(sketch, "E8.20", {"start": v(7.2, -19.29) * mm, "end": v(4.38, -20.12) * mm});
            skLineSegment(sketch, "E8.21", {"start": v(4.38, -20.12) * mm, "end": v(1.47, -20.53) * mm});
            skLineSegment(sketch, "E8.22", {"start": v(1.47, -20.53) * mm, "end": v(-1.47, -20.53) * mm});
            skLineSegment(sketch, "E8.23", {"start": v(-1.47, -20.53) * mm, "end": v(-4.38, -20.12) * mm});
            skLineSegment(sketch, "E8.24", {"start": v(-4.38, -20.12) * mm, "end": v(-7.2, -19.29) * mm});
            skLineSegment(sketch, "E8.25", {"start": v(-7.2, -19.29) * mm, "end": v(-9.87, -18.07) * mm});
            skLineSegment(sketch, "E8.26", {"start": v(-9.87, -18.07) * mm, "end": v(-12.34, -16.48) * mm});
            skLineSegment(sketch, "E8.27", {"start": v(-12.34, -16.48) * mm, "end": v(-14.56, -14.56) * mm});
            skLineSegment(sketch, "E8.28", {"start": v(-14.56, -14.56) * mm, "end": v(-16.48, -12.34) * mm});
            skLineSegment(sketch, "E8.29", {"start": v(-16.48, -12.34) * mm, "end": v(-18.07, -9.87) * mm});
            skLineSegment(sketch, "E8.30", {"start": v(-18.07, -9.87) * mm, "end": v(-19.29, -7.2) * mm});
            skLineSegment(sketch, "E8.31", {"start": v(-19.29, -7.2) * mm, "end": v(-20.12, -4.38) * mm});
            skLineSegment(sketch, "E8.32", {"start": v(-20.12, -4.38) * mm, "end": v(-20.53, -1.47) * mm});
            skLineSegment(sketch, "E8.33", {"start": v(-20.53, -1.47) * mm, "end": v(-20.53, 1.47) * mm});
            skLineSegment(sketch, "E8.34", {"start": v(-20.53, 1.47) * mm, "end": v(-20.12, 4.38) * mm});
            skLineSegment(sketch, "E8.35", {"start": v(-20.12, 4.38) * mm, "end": v(-19.29, 7.2) * mm});
            skLineSegment(sketch, "E8.36", {"start": v(-19.29, 7.2) * mm, "end": v(-18.07, 9.87) * mm});
            skLineSegment(sketch, "E8.37", {"start": v(-18.07, 9.87) * mm, "end": v(-16.48, 12.34) * mm});
            skLineSegment(sketch, "E8.38", {"start": v(-16.48, 12.34) * mm, "end": v(-14.56, 14.56) * mm});
            skLineSegment(sketch, "E8.39", {"start": v(-14.56, 14.56) * mm, "end": v(-12.34, 16.48) * mm});
            skLineSegment(sketch, "E8.40", {"start": v(-12.34, 16.48) * mm, "end": v(-9.87, 18.07) * mm});
            skLineSegment(sketch, "E8.41", {"start": v(-9.87, 18.07) * mm, "end": v(-7.2, 19.29) * mm});
            skLineSegment(sketch, "E8.42", {"start": v(-7.2, 19.29) * mm, "end": v(-4.38, 20.12) * mm});
            skLineSegment(sketch, "E8.43", {"start": v(-4.38, 20.12) * mm, "end": v(-1.47, 20.53) * mm});
            skPoint(sketch, "E8.0.midPoint", {"position": v(0, 20.53) * mm});
            skSolve(sketch);
        }
        {
            var Q1;
            Q1=makeQuery(id+"F18.opLoft","CAP_FACE",FACE,{"disambiguationData":[OSD([makeQuery(id+"F17.imprint","IMPRINT",FACE,{"disambiguationData":[TD([[makeQuery(id+"F17.imprint","IMPRINT",EDGE,{"derivedFrom":sQuery(id+"F17.wireOp",EDGE,"E7.0")}),-1.0]])]})])],"isStart":true});
            var Q2;
            Q2=makeQuery(id+"F20.imprint","IMPRINT",FACE,{"disambiguationData":[TD([[makeQuery(id+"F20.imprint","IMPRINT",EDGE,{"derivedFrom":sQuery(id+"F20.wireOp",EDGE,"E8.0")}),-1.0]])]});
            loft(context, id + "F21", {"operationType" : NewBodyOperationType.ADD, "sheetProfilesArray" : [{ "sheetProfileEntities" : qUnion([Q1]) }, { "sheetProfileEntities" : qUnion([Q2]) }]});
        }
        {
            var Q0;
            Q0=qCreatedBy(id+"F19.planeOp",FACE);
            cPlane(context, id + "F22", {"entities" : qUnion([Q0]), "cplaneType" : CPlaneType.OFFSET, "offset" : 2.54 * mm, "width" : 152.4 * mm, "height" : 152.4 * mm});
        }
        {
            var Q0;
            Q0=qCreatedBy(id+"F22.planeOp",FACE);
            var sketch = newSketch(context, id + "F23", { "sketchPlane" : qUnion([Q0])});
            skCircle(sketch, "E9.cCircle", {"center": v(0, 0) * mm, "radius": 21.8 * mm, "construction": true});
            skLineSegment(sketch, "E9.0", {"start": v(-1.6, 21.8) * mm, "end": v(1.6, 21.8) * mm});
            skLineSegment(sketch, "E9.1", {"start": v(1.6, 21.8) * mm, "end": v(4.75, 21.34) * mm});
            skLineSegment(sketch, "E9.2", {"start": v(4.75, 21.34) * mm, "end": v(7.81, 20.42) * mm});
            skLineSegment(sketch, "E9.3", {"start": v(7.81, 20.42) * mm, "end": v(10.7, 19.07) * mm});
            skLineSegment(sketch, "E9.4", {"start": v(10.7, 19.07) * mm, "end": v(13.36, 17.3) * mm});
            skLineSegment(sketch, "E9.5", {"start": v(13.36, 17.3) * mm, "end": v(15.74, 15.18) * mm});
            skLineSegment(sketch, "E9.6", {"start": v(15.74, 15.18) * mm, "end": v(17.78, 12.72) * mm});
            skLineSegment(sketch, "E9.7", {"start": v(17.78, 12.72) * mm, "end": v(19.45, 10) * mm});
            skLineSegment(sketch, "E9.8", {"start": v(19.45, 10) * mm, "end": v(20.7, 7.06) * mm});
            skLineSegment(sketch, "E9.9", {"start": v(20.7, 7.06) * mm, "end": v(21.5, 3.97) * mm});
            skLineSegment(sketch, "E9.10", {"start": v(21.5, 3.97) * mm, "end": v(21.85, 0.8) * mm});
            skLineSegment(sketch, "E9.11", {"start": v(21.85, 0.8) * mm, "end": v(21.74, -2.4) * mm});
            skLineSegment(sketch, "E9.12", {"start": v(21.74, -2.4) * mm, "end": v(21.16, -5.53) * mm});
            skLineSegment(sketch, "E9.13", {"start": v(21.16, -5.53) * mm, "end": v(20.12, -8.55) * mm});
            skLineSegment(sketch, "E9.14", {"start": v(20.12, -8.55) * mm, "end": v(18.66, -11.4) * mm});
            skLineSegment(sketch, "E9.15", {"start": v(18.66, -11.4) * mm, "end": v(16.8, -13.99) * mm});
            skLineSegment(sketch, "E9.16", {"start": v(16.8, -13.99) * mm, "end": v(14.6, -16.29) * mm});
            skLineSegment(sketch, "E9.17", {"start": v(14.6, -16.29) * mm, "end": v(12.07, -18.24) * mm});
            skLineSegment(sketch, "E9.18", {"start": v(12.07, -18.24) * mm, "end": v(9.28, -19.8) * mm});
            skLineSegment(sketch, "E9.19", {"start": v(9.28, -19.8) * mm, "end": v(6.3, -20.94) * mm});
            skLineSegment(sketch, "E9.20", {"start": v(6.3, -20.94) * mm, "end": v(3.18, -21.63) * mm});
            skLineSegment(sketch, "E9.21", {"start": v(3.18, -21.63) * mm, "end": v(0, -21.87) * mm});
            skLineSegment(sketch, "E9.22", {"start": v(0, -21.87) * mm, "end": v(-3.18, -21.63) * mm});
            skLineSegment(sketch, "E9.23", {"start": v(-3.18, -21.63) * mm, "end": v(-6.3, -20.94) * mm});
            skLineSegment(sketch, "E9.24", {"start": v(-6.3, -20.94) * mm, "end": v(-9.28, -19.8) * mm});
            skLineSegment(sketch, "E9.25", {"start": v(-9.28, -19.8) * mm, "end": v(-12.07, -18.24) * mm});
            skLineSegment(sketch, "E9.26", {"start": v(-12.07, -18.24) * mm, "end": v(-14.6, -16.29) * mm});
            skLineSegment(sketch, "E9.27", {"start": v(-14.6, -16.29) * mm, "end": v(-16.8, -13.99) * mm});
            skLineSegment(sketch, "E9.28", {"start": v(-16.8, -13.99) * mm, "end": v(-18.66, -11.4) * mm});
            skLineSegment(sketch, "E9.29", {"start": v(-18.66, -11.4) * mm, "end": v(-20.12, -8.55) * mm});
            skLineSegment(sketch, "E9.30", {"start": v(-20.12, -8.55) * mm, "end": v(-21.16, -5.53) * mm});
            skLineSegment(sketch, "E9.31", {"start": v(-21.16, -5.53) * mm, "end": v(-21.74, -2.4) * mm});
            skLineSegment(sketch, "E9.32", {"start": v(-21.74, -2.4) * mm, "end": v(-21.85, 0.8) * mm});
            skLineSegment(sketch, "E9.33", {"start": v(-21.85, 0.8) * mm, "end": v(-21.5, 3.97) * mm});
            skLineSegment(sketch, "E9.34", {"start": v(-21.5, 3.97) * mm, "end": v(-20.7, 7.06) * mm});
            skLineSegment(sketch, "E9.35", {"start": v(-20.7, 7.06) * mm, "end": v(-19.45, 10) * mm});
            skLineSegment(sketch, "E9.36", {"start": v(-19.45, 10) * mm, "end": v(-17.78, 12.72) * mm});
            skLineSegment(sketch, "E9.37", {"start": v(-17.78, 12.72) * mm, "end": v(-15.74, 15.18) * mm});
            skLineSegment(sketch, "E9.38", {"start": v(-15.74, 15.18) * mm, "end": v(-13.36, 17.3) * mm});
            skLineSegment(sketch, "E9.39", {"start": v(-13.36, 17.3) * mm, "end": v(-10.7, 19.07) * mm});
            skLineSegment(sketch, "E9.40", {"start": v(-10.7, 19.07) * mm, "end": v(-7.81, 20.42) * mm});
            skLineSegment(sketch, "E9.41", {"start": v(-7.81, 20.42) * mm, "end": v(-4.75, 21.34) * mm});
            skLineSegment(sketch, "E9.42", {"start": v(-4.75, 21.34) * mm, "end": v(-1.6, 21.8) * mm});
            skPoint(sketch, "E9.0.midPoint", {"position": v(0, 21.8) * mm});
            skSolve(sketch);
        }
        {
            var Q1;
            Q1=makeQuery(id+"F21.opLoft","CAP_FACE",FACE,{"disambiguationData":[OSD([makeQuery(id+"F20.imprint","IMPRINT",FACE,{"disambiguationData":[TD([[makeQuery(id+"F20.imprint","IMPRINT",EDGE,{"derivedFrom":sQuery(id+"F20.wireOp",EDGE,"E8.0")}),-1.0]])]})])],"isStart":true});
            var Q2;
            Q2=makeQuery(id+"F23.imprint","IMPRINT",FACE,{"disambiguationData":[TD([[makeQuery(id+"F23.imprint","IMPRINT",EDGE,{"derivedFrom":sQuery(id+"F23.wireOp",EDGE,"E9.0")}),-1.0]])]});
            loft(context, id + "F24", {"operationType" : NewBodyOperationType.ADD, "sheetProfilesArray" : [{ "sheetProfileEntities" : qUnion([Q1]) }, { "sheetProfileEntities" : qUnion([Q2]) }]});
        }
        {
            var Q0;
            Q0=qCreatedBy(id+"F22.planeOp",FACE);
            cPlane(context, id + "F25", {"entities" : qUnion([Q0]), "cplaneType" : CPlaneType.OFFSET, "offset" : 2.54 * mm, "width" : 152.4 * mm, "height" : 152.4 * mm});
        }
        {
            var Q0;
            Q0=qCreatedBy(id+"F25.planeOp",FACE);
            var sketch = newSketch(context, id + "F26", { "sketchPlane" : qUnion([Q0])});
            skCircle(sketch, "E10.cCircle", {"center": v(0, 0) * mm, "radius": 22.94 * mm, "construction": true});
            skLineSegment(sketch, "E10.0", {"start": v(-1.72, 22.94) * mm, "end": v(1.72, 22.94) * mm});
            skLineSegment(sketch, "E10.1", {"start": v(1.72, 22.94) * mm, "end": v(5.12, 22.43) * mm});
            skLineSegment(sketch, "E10.2", {"start": v(5.12, 22.43) * mm, "end": v(8.4, 21.41) * mm});
            skLineSegment(sketch, "E10.3", {"start": v(8.4, 21.41) * mm, "end": v(11.5, 19.92) * mm});
            skLineSegment(sketch, "E10.4", {"start": v(11.5, 19.92) * mm, "end": v(14.34, 17.99) * mm});
            skLineSegment(sketch, "E10.5", {"start": v(14.34, 17.99) * mm, "end": v(16.86, 15.65) * mm});
            skLineSegment(sketch, "E10.6", {"start": v(16.86, 15.65) * mm, "end": v(19, 12.96) * mm});
            skLineSegment(sketch, "E10.7", {"start": v(19, 12.96) * mm, "end": v(20.73, 9.98) * mm});
            skLineSegment(sketch, "E10.8", {"start": v(20.73, 9.98) * mm, "end": v(21.98, 6.78) * mm});
            skLineSegment(sketch, "E10.9", {"start": v(21.98, 6.78) * mm, "end": v(22.75, 3.43) * mm});
            skLineSegment(sketch, "E10.10", {"start": v(22.75, 3.43) * mm, "end": v(23, 0) * mm});
            skLineSegment(sketch, "E10.11", {"start": v(23, 0) * mm, "end": v(22.75, -3.43) * mm});
            skLineSegment(sketch, "E10.12", {"start": v(22.75, -3.43) * mm, "end": v(21.98, -6.78) * mm});
            skLineSegment(sketch, "E10.13", {"start": v(21.98, -6.78) * mm, "end": v(20.73, -9.98) * mm});
            skLineSegment(sketch, "E10.14", {"start": v(20.73, -9.98) * mm, "end": v(19, -12.96) * mm});
            skLineSegment(sketch, "E10.15", {"start": v(19, -12.96) * mm, "end": v(16.86, -15.65) * mm});
            skLineSegment(sketch, "E10.16", {"start": v(16.86, -15.65) * mm, "end": v(14.34, -17.99) * mm});
            skLineSegment(sketch, "E10.17", {"start": v(14.34, -17.99) * mm, "end": v(11.5, -19.92) * mm});
            skLineSegment(sketch, "E10.18", {"start": v(11.5, -19.92) * mm, "end": v(8.4, -21.41) * mm});
            skLineSegment(sketch, "E10.19", {"start": v(8.4, -21.41) * mm, "end": v(5.12, -22.43) * mm});
            skLineSegment(sketch, "E10.20", {"start": v(5.12, -22.43) * mm, "end": v(1.72, -22.94) * mm});
            skLineSegment(sketch, "E10.21", {"start": v(1.72, -22.94) * mm, "end": v(-1.72, -22.94) * mm});
            skLineSegment(sketch, "E10.22", {"start": v(-1.72, -22.94) * mm, "end": v(-5.12, -22.43) * mm});
            skLineSegment(sketch, "E10.23", {"start": v(-5.12, -22.43) * mm, "end": v(-8.4, -21.41) * mm});
            skLineSegment(sketch, "E10.24", {"start": v(-8.4, -21.41) * mm, "end": v(-11.5, -19.92) * mm});
            skLineSegment(sketch, "E10.25", {"start": v(-11.5, -19.92) * mm, "end": v(-14.34, -17.99) * mm});
            skLineSegment(sketch, "E10.26", {"start": v(-14.34, -17.99) * mm, "end": v(-16.86, -15.65) * mm});
            skLineSegment(sketch, "E10.27", {"start": v(-16.86, -15.65) * mm, "end": v(-19, -12.96) * mm});
            skLineSegment(sketch, "E10.28", {"start": v(-19, -12.96) * mm, "end": v(-20.73, -9.98) * mm});
            skLineSegment(sketch, "E10.29", {"start": v(-20.73, -9.98) * mm, "end": v(-21.98, -6.78) * mm});
            skLineSegment(sketch, "E10.30", {"start": v(-21.98, -6.78) * mm, "end": v(-22.75, -3.43) * mm});
            skLineSegment(sketch, "E10.31", {"start": v(-22.75, -3.43) * mm, "end": v(-23, 0) * mm});
            skLineSegment(sketch, "E10.32", {"start": v(-23, 0) * mm, "end": v(-22.75, 3.43) * mm});
            skLineSegment(sketch, "E10.33", {"start": v(-22.75, 3.43) * mm, "end": v(-21.98, 6.78) * mm});
            skLineSegment(sketch, "E10.34", {"start": v(-21.98, 6.78) * mm, "end": v(-20.73, 9.98) * mm});
            skLineSegment(sketch, "E10.35", {"start": v(-20.73, 9.98) * mm, "end": v(-19, 12.96) * mm});
            skLineSegment(sketch, "E10.36", {"start": v(-19, 12.96) * mm, "end": v(-16.86, 15.65) * mm});
            skLineSegment(sketch, "E10.37", {"start": v(-16.86, 15.65) * mm, "end": v(-14.34, 17.99) * mm});
            skLineSegment(sketch, "E10.38", {"start": v(-14.34, 17.99) * mm, "end": v(-11.5, 19.92) * mm});
            skLineSegment(sketch, "E10.39", {"start": v(-11.5, 19.92) * mm, "end": v(-8.4, 21.41) * mm});
            skLineSegment(sketch, "E10.40", {"start": v(-8.4, 21.41) * mm, "end": v(-5.12, 22.43) * mm});
            skLineSegment(sketch, "E10.41", {"start": v(-5.12, 22.43) * mm, "end": v(-1.72, 22.94) * mm});
            skPoint(sketch, "E10.0.midPoint", {"position": v(0, 22.94) * mm});
            skSolve(sketch);
        }
        {
            var Q1;
            Q1=makeQuery(id+"F24.opLoft","CAP_FACE",FACE,{"disambiguationData":[OSD([makeQuery(id+"F23.imprint","IMPRINT",FACE,{"disambiguationData":[TD([[makeQuery(id+"F23.imprint","IMPRINT",EDGE,{"derivedFrom":sQuery(id+"F23.wireOp",EDGE,"E9.0")}),-1.0]])]})])],"isStart":true});
            var Q2;
            Q2=makeQuery(id+"F26.imprint","IMPRINT",FACE,{"disambiguationData":[TD([[makeQuery(id+"F26.imprint","IMPRINT",EDGE,{"derivedFrom":sQuery(id+"F26.wireOp",EDGE,"E10.0")}),-1.0]])]});
            loft(context, id + "F27", {"operationType" : NewBodyOperationType.ADD, "sheetProfilesArray" : [{ "sheetProfileEntities" : qUnion([Q1]) }, { "sheetProfileEntities" : qUnion([Q2]) }]});
        }
        {
            var Q0;
            Q0=qCreatedBy(id+"F25.planeOp",FACE);
            cPlane(context, id + "F28", {"entities" : qUnion([Q0]), "cplaneType" : CPlaneType.OFFSET, "offset" : 2.54 * mm, "width" : 152.4 * mm, "height" : 152.4 * mm});
        }
        {
            var Q0;
            Q0=qCreatedBy(id+"F28.planeOp",FACE);
            var sketch = newSketch(context, id + "F29", { "sketchPlane" : qUnion([Q0])});
            skCircle(sketch, "E11.cCircle", {"center": v(0, 0) * mm, "radius": 24.07 * mm, "construction": true});
            skLineSegment(sketch, "E11.0", {"start": v(-1.85, 24.07) * mm, "end": v(1.85, 24.07) * mm});
            skLineSegment(sketch, "E11.1", {"start": v(1.85, 24.07) * mm, "end": v(5.5, 23.5) * mm});
            skLineSegment(sketch, "E11.2", {"start": v(5.5, 23.5) * mm, "end": v(9.03, 22.4) * mm});
            skLineSegment(sketch, "E11.3", {"start": v(9.03, 22.4) * mm, "end": v(12.34, 20.75) * mm});
            skLineSegment(sketch, "E11.4", {"start": v(12.34, 20.75) * mm, "end": v(15.36, 18.63) * mm});
            skLineSegment(sketch, "E11.5", {"start": v(15.36, 18.63) * mm, "end": v(18.03, 16.06) * mm});
            skLineSegment(sketch, "E11.6", {"start": v(18.03, 16.06) * mm, "end": v(20.27, 13.12) * mm});
            skLineSegment(sketch, "E11.7", {"start": v(20.27, 13.12) * mm, "end": v(22.03, 9.88) * mm});
            skLineSegment(sketch, "E11.8", {"start": v(22.03, 9.88) * mm, "end": v(23.28, 6.4) * mm});
            skLineSegment(sketch, "E11.9", {"start": v(23.28, 6.4) * mm, "end": v(23.99, 2.77) * mm});
            skLineSegment(sketch, "E11.10", {"start": v(23.99, 2.77) * mm, "end": v(24.13, -0.92) * mm});
            skLineSegment(sketch, "E11.11", {"start": v(24.13, -0.92) * mm, "end": v(23.7, -4.6) * mm});
            skLineSegment(sketch, "E11.12", {"start": v(23.7, -4.6) * mm, "end": v(22.72, -8.16) * mm});
            skLineSegment(sketch, "E11.13", {"start": v(22.72, -8.16) * mm, "end": v(21.21, -11.53) * mm});
            skLineSegment(sketch, "E11.14", {"start": v(21.21, -11.53) * mm, "end": v(19.2, -14.64) * mm});
            skLineSegment(sketch, "E11.15", {"start": v(19.2, -14.64) * mm, "end": v(16.74, -17.4) * mm});
            skLineSegment(sketch, "E11.16", {"start": v(16.74, -17.4) * mm, "end": v(13.9, -19.75) * mm});
            skLineSegment(sketch, "E11.17", {"start": v(13.9, -19.75) * mm, "end": v(10.71, -21.64) * mm});
            skLineSegment(sketch, "E11.18", {"start": v(10.71, -21.64) * mm, "end": v(7.28, -23.02) * mm});
            skLineSegment(sketch, "E11.19", {"start": v(7.28, -23.02) * mm, "end": v(3.69, -23.86) * mm});
            skLineSegment(sketch, "E11.20", {"start": v(3.69, -23.86) * mm, "end": v(0, -24.14) * mm});
            skLineSegment(sketch, "E11.21", {"start": v(0, -24.14) * mm, "end": v(-3.69, -23.86) * mm});
            skLineSegment(sketch, "E11.22", {"start": v(-3.69, -23.86) * mm, "end": v(-7.28, -23.02) * mm});
            skLineSegment(sketch, "E11.23", {"start": v(-7.28, -23.02) * mm, "end": v(-10.71, -21.64) * mm});
            skLineSegment(sketch, "E11.24", {"start": v(-10.71, -21.64) * mm, "end": v(-13.9, -19.75) * mm});
            skLineSegment(sketch, "E11.25", {"start": v(-13.9, -19.75) * mm, "end": v(-16.74, -17.4) * mm});
            skLineSegment(sketch, "E11.26", {"start": v(-16.74, -17.4) * mm, "end": v(-19.2, -14.64) * mm});
            skLineSegment(sketch, "E11.27", {"start": v(-19.2, -14.64) * mm, "end": v(-21.21, -11.53) * mm});
            skLineSegment(sketch, "E11.28", {"start": v(-21.21, -11.53) * mm, "end": v(-22.72, -8.16) * mm});
            skLineSegment(sketch, "E11.29", {"start": v(-22.72, -8.16) * mm, "end": v(-23.7, -4.6) * mm});
            skLineSegment(sketch, "E11.30", {"start": v(-23.7, -4.6) * mm, "end": v(-24.13, -0.92) * mm});
            skLineSegment(sketch, "E11.31", {"start": v(-24.13, -0.92) * mm, "end": v(-23.99, 2.77) * mm});
            skLineSegment(sketch, "E11.32", {"start": v(-23.99, 2.77) * mm, "end": v(-23.28, 6.4) * mm});
            skLineSegment(sketch, "E11.33", {"start": v(-23.28, 6.4) * mm, "end": v(-22.03, 9.88) * mm});
            skLineSegment(sketch, "E11.34", {"start": v(-22.03, 9.88) * mm, "end": v(-20.27, 13.12) * mm});
            skLineSegment(sketch, "E11.35", {"start": v(-20.27, 13.12) * mm, "end": v(-18.03, 16.06) * mm});
            skLineSegment(sketch, "E11.36", {"start": v(-18.03, 16.06) * mm, "end": v(-15.36, 18.63) * mm});
            skLineSegment(sketch, "E11.37", {"start": v(-15.36, 18.63) * mm, "end": v(-12.34, 20.75) * mm});
            skLineSegment(sketch, "E11.38", {"start": v(-12.34, 20.75) * mm, "end": v(-9.03, 22.4) * mm});
            skLineSegment(sketch, "E11.39", {"start": v(-9.03, 22.4) * mm, "end": v(-5.5, 23.5) * mm});
            skLineSegment(sketch, "E11.40", {"start": v(-5.5, 23.5) * mm, "end": v(-1.85, 24.07) * mm});
            skPoint(sketch, "E11.0.midPoint", {"position": v(0, 24.07) * mm});
            skSolve(sketch);
        }
        {
            var Q1;
            Q1=makeQuery(id+"F27.opLoft","CAP_FACE",FACE,{"disambiguationData":[OSD([makeQuery(id+"F26.imprint","IMPRINT",FACE,{"disambiguationData":[TD([[makeQuery(id+"F26.imprint","IMPRINT",EDGE,{"derivedFrom":sQuery(id+"F26.wireOp",EDGE,"E10.0")}),-1.0]])]})])],"isStart":true});
            var Q2;
            Q2=makeQuery(id+"F29.imprint","IMPRINT",FACE,{"disambiguationData":[TD([[makeQuery(id+"F29.imprint","IMPRINT",EDGE,{"derivedFrom":sQuery(id+"F29.wireOp",EDGE,"E11.0")}),-1.0]])]});
            loft(context, id + "F30", {"operationType" : NewBodyOperationType.ADD, "sheetProfilesArray" : [{ "sheetProfileEntities" : qUnion([Q1]) }, { "sheetProfileEntities" : qUnion([Q2]) }]});
        }
        {
            var Q0;
            Q0=qCreatedBy(id+"F28.planeOp",FACE);
            cPlane(context, id + "F31", {"entities" : qUnion([Q0]), "cplaneType" : CPlaneType.OFFSET, "offset" : 2.54 * mm, "width" : 152.4 * mm, "height" : 152.4 * mm});
        }
        {
            var Q0;
            Q0=qCreatedBy(id+"F31.planeOp",FACE);
            var sketch = newSketch(context, id + "F32", { "sketchPlane" : qUnion([Q0])});
            skCircle(sketch, "E12.cCircle", {"center": v(0, 0) * mm, "radius": 25.2 * mm, "construction": true});
            skLineSegment(sketch, "E12.0", {"start": v(-1.98, 25.2) * mm, "end": v(1.98, 25.2) * mm});
            skLineSegment(sketch, "E12.1", {"start": v(1.98, 25.2) * mm, "end": v(5.9, 24.59) * mm});
            skLineSegment(sketch, "E12.2", {"start": v(5.9, 24.59) * mm, "end": v(9.68, 23.36) * mm});
            skLineSegment(sketch, "E12.3", {"start": v(9.68, 23.36) * mm, "end": v(13.21, 21.56) * mm});
            skLineSegment(sketch, "E12.4", {"start": v(13.21, 21.56) * mm, "end": v(16.42, 19.23) * mm});
            skLineSegment(sketch, "E12.5", {"start": v(16.42, 19.23) * mm, "end": v(19.23, 16.42) * mm});
            skLineSegment(sketch, "E12.6", {"start": v(19.23, 16.42) * mm, "end": v(21.56, 13.21) * mm});
            skLineSegment(sketch, "E12.7", {"start": v(21.56, 13.21) * mm, "end": v(23.36, 9.68) * mm});
            skLineSegment(sketch, "E12.8", {"start": v(23.36, 9.68) * mm, "end": v(24.59, 5.9) * mm});
            skLineSegment(sketch, "E12.9", {"start": v(24.59, 5.9) * mm, "end": v(25.2, 1.98) * mm});
            skLineSegment(sketch, "E12.10", {"start": v(25.2, 1.98) * mm, "end": v(25.2, -1.98) * mm});
            skLineSegment(sketch, "E12.11", {"start": v(25.2, -1.98) * mm, "end": v(24.59, -5.9) * mm});
            skLineSegment(sketch, "E12.12", {"start": v(24.59, -5.9) * mm, "end": v(23.36, -9.68) * mm});
            skLineSegment(sketch, "E12.13", {"start": v(23.36, -9.68) * mm, "end": v(21.56, -13.21) * mm});
            skLineSegment(sketch, "E12.14", {"start": v(21.56, -13.21) * mm, "end": v(19.23, -16.42) * mm});
            skLineSegment(sketch, "E12.15", {"start": v(19.23, -16.42) * mm, "end": v(16.42, -19.23) * mm});
            skLineSegment(sketch, "E12.16", {"start": v(16.42, -19.23) * mm, "end": v(13.21, -21.56) * mm});
            skLineSegment(sketch, "E12.17", {"start": v(13.21, -21.56) * mm, "end": v(9.68, -23.36) * mm});
            skLineSegment(sketch, "E12.18", {"start": v(9.68, -23.36) * mm, "end": v(5.9, -24.59) * mm});
            skLineSegment(sketch, "E12.19", {"start": v(5.9, -24.59) * mm, "end": v(1.98, -25.2) * mm});
            skLineSegment(sketch, "E12.20", {"start": v(1.98, -25.2) * mm, "end": v(-1.98, -25.2) * mm});
            skLineSegment(sketch, "E12.21", {"start": v(-1.98, -25.2) * mm, "end": v(-5.9, -24.59) * mm});
            skLineSegment(sketch, "E12.22", {"start": v(-5.9, -24.59) * mm, "end": v(-9.68, -23.36) * mm});
            skLineSegment(sketch, "E12.23", {"start": v(-9.68, -23.36) * mm, "end": v(-13.21, -21.56) * mm});
            skLineSegment(sketch, "E12.24", {"start": v(-13.21, -21.56) * mm, "end": v(-16.42, -19.23) * mm});
            skLineSegment(sketch, "E12.25", {"start": v(-16.42, -19.23) * mm, "end": v(-19.23, -16.42) * mm});
            skLineSegment(sketch, "E12.26", {"start": v(-19.23, -16.42) * mm, "end": v(-21.56, -13.21) * mm});
            skLineSegment(sketch, "E12.27", {"start": v(-21.56, -13.21) * mm, "end": v(-23.36, -9.68) * mm});
            skLineSegment(sketch, "E12.28", {"start": v(-23.36, -9.68) * mm, "end": v(-24.59, -5.9) * mm});
            skLineSegment(sketch, "E12.29", {"start": v(-24.59, -5.9) * mm, "end": v(-25.2, -1.98) * mm});
            skLineSegment(sketch, "E12.30", {"start": v(-25.2, -1.98) * mm, "end": v(-25.2, 1.98) * mm});
            skLineSegment(sketch, "E12.31", {"start": v(-25.2, 1.98) * mm, "end": v(-24.59, 5.9) * mm});
            skLineSegment(sketch, "E12.32", {"start": v(-24.59, 5.9) * mm, "end": v(-23.36, 9.68) * mm});
            skLineSegment(sketch, "E12.33", {"start": v(-23.36, 9.68) * mm, "end": v(-21.56, 13.21) * mm});
            skLineSegment(sketch, "E12.34", {"start": v(-21.56, 13.21) * mm, "end": v(-19.23, 16.42) * mm});
            skLineSegment(sketch, "E12.35", {"start": v(-19.23, 16.42) * mm, "end": v(-16.42, 19.23) * mm});
            skLineSegment(sketch, "E12.36", {"start": v(-16.42, 19.23) * mm, "end": v(-13.21, 21.56) * mm});
            skLineSegment(sketch, "E12.37", {"start": v(-13.21, 21.56) * mm, "end": v(-9.68, 23.36) * mm});
            skLineSegment(sketch, "E12.38", {"start": v(-9.68, 23.36) * mm, "end": v(-5.9, 24.59) * mm});
            skLineSegment(sketch, "E12.39", {"start": v(-5.9, 24.59) * mm, "end": v(-1.98, 25.2) * mm});
            skPoint(sketch, "E12.0.midPoint", {"position": v(0, 25.2) * mm});
            skSolve(sketch);
        }
        {
            var Q1;
            Q1=makeQuery(id+"F30.opLoft","CAP_FACE",FACE,{"disambiguationData":[OSD([makeQuery(id+"F29.imprint","IMPRINT",FACE,{"disambiguationData":[TD([[makeQuery(id+"F29.imprint","IMPRINT",EDGE,{"derivedFrom":sQuery(id+"F29.wireOp",EDGE,"E11.0")}),-1.0]])]})])],"isStart":true});
            var Q2;
            Q2=makeQuery(id+"F32.imprint","IMPRINT",FACE,{"disambiguationData":[TD([[makeQuery(id+"F32.imprint","IMPRINT",EDGE,{"derivedFrom":sQuery(id+"F32.wireOp",EDGE,"E12.0")}),-1.0]])]});
            loft(context, id + "F33", {"operationType" : NewBodyOperationType.ADD, "sheetProfilesArray" : [{ "sheetProfileEntities" : qUnion([Q1]) }, { "sheetProfileEntities" : qUnion([Q2]) }]});
        }
        {
            var Q0;
            Q0=qCreatedBy(id+"F31.planeOp",FACE);
            cPlane(context, id + "F34", {"entities" : qUnion([Q0]), "cplaneType" : CPlaneType.OFFSET, "offset" : 2.54 * mm, "width" : 152.4 * mm, "height" : 152.4 * mm});
        }
        {
            var Q0;
            Q0=qCreatedBy(id+"F34.planeOp",FACE);
            var sketch = newSketch(context, id + "F35", { "sketchPlane" : qUnion([Q0])});
            skCircle(sketch, "E13.cCircle", {"center": v(0, 0) * mm, "radius": 26.48 * mm, "construction": true});
            skLineSegment(sketch, "E13.0", {"start": v(-2.14, 26.48) * mm, "end": v(2.14, 26.48) * mm});
            skLineSegment(sketch, "E13.1", {"start": v(2.14, 26.48) * mm, "end": v(6.36, 25.8) * mm});
            skLineSegment(sketch, "E13.2", {"start": v(6.36, 25.8) * mm, "end": v(10.41, 24.44) * mm});
            skLineSegment(sketch, "E13.3", {"start": v(10.41, 24.44) * mm, "end": v(14.2, 22.45) * mm});
            skLineSegment(sketch, "E13.4", {"start": v(14.2, 22.45) * mm, "end": v(17.62, 19.89) * mm});
            skLineSegment(sketch, "E13.5", {"start": v(17.62, 19.89) * mm, "end": v(20.58, 16.8) * mm});
            skLineSegment(sketch, "E13.6", {"start": v(20.58, 16.8) * mm, "end": v(23, 13.28) * mm});
            skLineSegment(sketch, "E13.7", {"start": v(23, 13.28) * mm, "end": v(24.84, 9.42) * mm});
            skLineSegment(sketch, "E13.8", {"start": v(24.84, 9.42) * mm, "end": v(26.03, 5.31) * mm});
            skLineSegment(sketch, "E13.9", {"start": v(26.03, 5.31) * mm, "end": v(26.55, 1.07) * mm});
            skLineSegment(sketch, "E13.10", {"start": v(26.55, 1.07) * mm, "end": v(26.37, -3.2) * mm});
            skLineSegment(sketch, "E13.11", {"start": v(26.37, -3.2) * mm, "end": v(25.52, -7.4) * mm});
            skLineSegment(sketch, "E13.12", {"start": v(25.52, -7.4) * mm, "end": v(24, -11.39) * mm});
            skLineSegment(sketch, "E13.13", {"start": v(24, -11.39) * mm, "end": v(21.86, -15.1) * mm});
            skLineSegment(sketch, "E13.14", {"start": v(21.86, -15.1) * mm, "end": v(19.16, -18.4) * mm});
            skLineSegment(sketch, "E13.15", {"start": v(19.16, -18.4) * mm, "end": v(15.96, -21.24) * mm});
            skLineSegment(sketch, "E13.16", {"start": v(15.96, -21.24) * mm, "end": v(12.35, -23.52) * mm});
            skLineSegment(sketch, "E13.17", {"start": v(12.35, -23.52) * mm, "end": v(8.41, -25.2) * mm});
            skLineSegment(sketch, "E13.18", {"start": v(8.41, -25.2) * mm, "end": v(4.26, -26.22) * mm});
            skLineSegment(sketch, "E13.19", {"start": v(4.26, -26.22) * mm, "end": v(0, -26.57) * mm});
            skLineSegment(sketch, "E13.20", {"start": v(0, -26.57) * mm, "end": v(-4.26, -26.22) * mm});
            skLineSegment(sketch, "E13.21", {"start": v(-4.26, -26.22) * mm, "end": v(-8.41, -25.2) * mm});
            skLineSegment(sketch, "E13.22", {"start": v(-8.41, -25.2) * mm, "end": v(-12.35, -23.52) * mm});
            skLineSegment(sketch, "E13.23", {"start": v(-12.35, -23.52) * mm, "end": v(-15.96, -21.24) * mm});
            skLineSegment(sketch, "E13.24", {"start": v(-15.96, -21.24) * mm, "end": v(-19.16, -18.4) * mm});
            skLineSegment(sketch, "E13.25", {"start": v(-19.16, -18.4) * mm, "end": v(-21.86, -15.1) * mm});
            skLineSegment(sketch, "E13.26", {"start": v(-21.86, -15.1) * mm, "end": v(-24, -11.39) * mm});
            skLineSegment(sketch, "E13.27", {"start": v(-24, -11.39) * mm, "end": v(-25.52, -7.4) * mm});
            skLineSegment(sketch, "E13.28", {"start": v(-25.52, -7.4) * mm, "end": v(-26.37, -3.2) * mm});
            skLineSegment(sketch, "E13.29", {"start": v(-26.37, -3.2) * mm, "end": v(-26.55, 1.07) * mm});
            skLineSegment(sketch, "E13.30", {"start": v(-26.55, 1.07) * mm, "end": v(-26.03, 5.31) * mm});
            skLineSegment(sketch, "E13.31", {"start": v(-26.03, 5.31) * mm, "end": v(-24.84, 9.42) * mm});
            skLineSegment(sketch, "E13.32", {"start": v(-24.84, 9.42) * mm, "end": v(-23, 13.28) * mm});
            skLineSegment(sketch, "E13.33", {"start": v(-23, 13.28) * mm, "end": v(-20.58, 16.8) * mm});
            skLineSegment(sketch, "E13.34", {"start": v(-20.58, 16.8) * mm, "end": v(-17.62, 19.89) * mm});
            skLineSegment(sketch, "E13.35", {"start": v(-17.62, 19.89) * mm, "end": v(-14.2, 22.45) * mm});
            skLineSegment(sketch, "E13.36", {"start": v(-14.2, 22.45) * mm, "end": v(-10.41, 24.44) * mm});
            skLineSegment(sketch, "E13.37", {"start": v(-10.41, 24.44) * mm, "end": v(-6.36, 25.8) * mm});
            skLineSegment(sketch, "E13.38", {"start": v(-6.36, 25.8) * mm, "end": v(-2.14, 26.48) * mm});
            skPoint(sketch, "E13.0.midPoint", {"position": v(0, 26.48) * mm});
            skSolve(sketch);
        }
        {
            var Q1;
            Q1=makeQuery(id+"F33.opLoft","CAP_FACE",FACE,{"disambiguationData":[OSD([makeQuery(id+"F32.imprint","IMPRINT",FACE,{"disambiguationData":[TD([[makeQuery(id+"F32.imprint","IMPRINT",EDGE,{"derivedFrom":sQuery(id+"F32.wireOp",EDGE,"E12.0")}),-1.0]])]})])],"isStart":true});
            var Q2;
            Q2=makeQuery(id+"F35.imprint","IMPRINT",FACE,{"disambiguationData":[TD([[makeQuery(id+"F35.imprint","IMPRINT",EDGE,{"derivedFrom":sQuery(id+"F35.wireOp",EDGE,"E13.0")}),-1.0]])]});
            loft(context, id + "F36", {"operationType" : NewBodyOperationType.ADD, "sheetProfilesArray" : [{ "sheetProfileEntities" : qUnion([Q1]) }, { "sheetProfileEntities" : qUnion([Q2]) }]});
        }
        {
            var Q0;
            Q0=qCreatedBy(id+"F34.planeOp",FACE);
            cPlane(context, id + "F37", {"entities" : qUnion([Q0]), "cplaneType" : CPlaneType.OFFSET, "offset" : 2.54 * mm, "width" : 152.4 * mm, "height" : 152.4 * mm});
        }
        {
            var Q0;
            Q0=qCreatedBy(id+"F37.planeOp",FACE);
            var sketch = newSketch(context, id + "F38", { "sketchPlane" : qUnion([Q0])});
            skCircle(sketch, "E14.cCircle", {"center": v(0, 0) * mm, "radius": 27.61 * mm, "construction": true});
            skLineSegment(sketch, "E14.0", {"start": v(-2.29, 27.61) * mm, "end": v(2.29, 27.61) * mm});
            skLineSegment(sketch, "E14.1", {"start": v(2.29, 27.61) * mm, "end": v(6.8, 26.86) * mm});
            skLineSegment(sketch, "E14.2", {"start": v(6.8, 26.86) * mm, "end": v(11.13, 25.37) * mm});
            skLineSegment(sketch, "E14.3", {"start": v(11.13, 25.37) * mm, "end": v(15.16, 23.2) * mm});
            skLineSegment(sketch, "E14.4", {"start": v(15.16, 23.2) * mm, "end": v(18.77, 20.39) * mm});
            skLineSegment(sketch, "E14.5", {"start": v(18.77, 20.39) * mm, "end": v(21.87, 17.02) * mm});
            skLineSegment(sketch, "E14.6", {"start": v(21.87, 17.02) * mm, "end": v(24.37, 13.19) * mm});
            skLineSegment(sketch, "E14.7", {"start": v(24.37, 13.19) * mm, "end": v(26.2, 9) * mm});
            skLineSegment(sketch, "E14.8", {"start": v(26.2, 9) * mm, "end": v(27.33, 4.56) * mm});
            skLineSegment(sketch, "E14.9", {"start": v(27.33, 4.56) * mm, "end": v(27.7, 0) * mm});
            skLineSegment(sketch, "E14.10", {"start": v(27.7, 0) * mm, "end": v(27.33, -4.56) * mm});
            skLineSegment(sketch, "E14.11", {"start": v(27.33, -4.56) * mm, "end": v(26.2, -9) * mm});
            skLineSegment(sketch, "E14.12", {"start": v(26.2, -9) * mm, "end": v(24.37, -13.19) * mm});
            skLineSegment(sketch, "E14.13", {"start": v(24.37, -13.19) * mm, "end": v(21.87, -17.02) * mm});
            skLineSegment(sketch, "E14.14", {"start": v(21.87, -17.02) * mm, "end": v(18.77, -20.39) * mm});
            skLineSegment(sketch, "E14.15", {"start": v(18.77, -20.39) * mm, "end": v(15.16, -23.2) * mm});
            skLineSegment(sketch, "E14.16", {"start": v(15.16, -23.2) * mm, "end": v(11.13, -25.37) * mm});
            skLineSegment(sketch, "E14.17", {"start": v(11.13, -25.37) * mm, "end": v(6.8, -26.86) * mm});
            skLineSegment(sketch, "E14.18", {"start": v(6.8, -26.86) * mm, "end": v(2.29, -27.61) * mm});
            skLineSegment(sketch, "E14.19", {"start": v(2.29, -27.61) * mm, "end": v(-2.29, -27.61) * mm});
            skLineSegment(sketch, "E14.20", {"start": v(-2.29, -27.61) * mm, "end": v(-6.8, -26.86) * mm});
            skLineSegment(sketch, "E14.21", {"start": v(-6.8, -26.86) * mm, "end": v(-11.13, -25.37) * mm});
            skLineSegment(sketch, "E14.22", {"start": v(-11.13, -25.37) * mm, "end": v(-15.16, -23.2) * mm});
            skLineSegment(sketch, "E14.23", {"start": v(-15.16, -23.2) * mm, "end": v(-18.77, -20.39) * mm});
            skLineSegment(sketch, "E14.24", {"start": v(-18.77, -20.39) * mm, "end": v(-21.87, -17.02) * mm});
            skLineSegment(sketch, "E14.25", {"start": v(-21.87, -17.02) * mm, "end": v(-24.37, -13.19) * mm});
            skLineSegment(sketch, "E14.26", {"start": v(-24.37, -13.19) * mm, "end": v(-26.2, -9) * mm});
            skLineSegment(sketch, "E14.27", {"start": v(-26.2, -9) * mm, "end": v(-27.33, -4.56) * mm});
            skLineSegment(sketch, "E14.28", {"start": v(-27.33, -4.56) * mm, "end": v(-27.7, 0) * mm});
            skLineSegment(sketch, "E14.29", {"start": v(-27.7, 0) * mm, "end": v(-27.33, 4.56) * mm});
            skLineSegment(sketch, "E14.30", {"start": v(-27.33, 4.56) * mm, "end": v(-26.2, 9) * mm});
            skLineSegment(sketch, "E14.31", {"start": v(-26.2, 9) * mm, "end": v(-24.37, 13.19) * mm});
            skLineSegment(sketch, "E14.32", {"start": v(-24.37, 13.19) * mm, "end": v(-21.87, 17.02) * mm});
            skLineSegment(sketch, "E14.33", {"start": v(-21.87, 17.02) * mm, "end": v(-18.77, 20.39) * mm});
            skLineSegment(sketch, "E14.34", {"start": v(-18.77, 20.39) * mm, "end": v(-15.16, 23.2) * mm});
            skLineSegment(sketch, "E14.35", {"start": v(-15.16, 23.2) * mm, "end": v(-11.13, 25.37) * mm});
            skLineSegment(sketch, "E14.36", {"start": v(-11.13, 25.37) * mm, "end": v(-6.8, 26.86) * mm});
            skLineSegment(sketch, "E14.37", {"start": v(-6.8, 26.86) * mm, "end": v(-2.29, 27.61) * mm});
            skPoint(sketch, "E14.0.midPoint", {"position": v(0, 27.61) * mm});
            skSolve(sketch);
        }
        {
            var Q1;
            Q1=makeQuery(id+"F36.opLoft","CAP_FACE",FACE,{"disambiguationData":[OSD([makeQuery(id+"F35.imprint","IMPRINT",FACE,{"disambiguationData":[TD([[makeQuery(id+"F35.imprint","IMPRINT",EDGE,{"derivedFrom":sQuery(id+"F35.wireOp",EDGE,"E13.0")}),-1.0]])]})])],"isStart":true});
            var Q2;
            Q2=makeQuery(id+"F38.imprint","IMPRINT",FACE,{"disambiguationData":[TD([[makeQuery(id+"F38.imprint","IMPRINT",EDGE,{"derivedFrom":sQuery(id+"F38.wireOp",EDGE,"E14.0")}),-1.0]])]});
            loft(context, id + "F39", {"operationType" : NewBodyOperationType.ADD, "sheetProfilesArray" : [{ "sheetProfileEntities" : qUnion([Q1]) }, { "sheetProfileEntities" : qUnion([Q2]) }]});
        }
        {
            var Q0;
            Q0=qCreatedBy(id+"F37.planeOp",FACE);
            cPlane(context, id + "F40", {"entities" : qUnion([Q0]), "cplaneType" : CPlaneType.OFFSET, "offset" : 2.54 * mm, "width" : 152.4 * mm, "height" : 152.4 * mm});
        }
        {
            var Q0;
            Q0=qCreatedBy(id+"F40.planeOp",FACE);
            var sketch = newSketch(context, id + "F41", { "sketchPlane" : qUnion([Q0])});
            skCircle(sketch, "E15.cCircle", {"center": v(0, 0) * mm, "radius": 29.03 * mm, "construction": true});
            skLineSegment(sketch, "E15.0", {"start": v(-2.47, 29.03) * mm, "end": v(2.47, 29.03) * mm});
            skLineSegment(sketch, "E15.1", {"start": v(2.47, 29.03) * mm, "end": v(7.34, 28.2) * mm});
            skLineSegment(sketch, "E15.2", {"start": v(7.34, 28.2) * mm, "end": v(12, 26.55) * mm});
            skLineSegment(sketch, "E15.3", {"start": v(12, 26.55) * mm, "end": v(16.31, 24.14) * mm});
            skLineSegment(sketch, "E15.4", {"start": v(16.31, 24.14) * mm, "end": v(20.16, 21.03) * mm});
            skLineSegment(sketch, "E15.5", {"start": v(20.16, 21.03) * mm, "end": v(23.42, 17.32) * mm});
            skLineSegment(sketch, "E15.6", {"start": v(23.42, 17.32) * mm, "end": v(26.02, 13.12) * mm});
            skLineSegment(sketch, "E15.7", {"start": v(26.02, 13.12) * mm, "end": v(27.86, 8.53) * mm});
            skLineSegment(sketch, "E15.8", {"start": v(27.86, 8.53) * mm, "end": v(28.9, 3.7) * mm});
            skLineSegment(sketch, "E15.9", {"start": v(28.9, 3.7) * mm, "end": v(29.1, -1.24) * mm});
            skLineSegment(sketch, "E15.10", {"start": v(29.1, -1.24) * mm, "end": v(28.48, -6.14) * mm});
            skLineSegment(sketch, "E15.11", {"start": v(28.48, -6.14) * mm, "end": v(27.03, -10.86) * mm});
            skLineSegment(sketch, "E15.12", {"start": v(27.03, -10.86) * mm, "end": v(24.8, -15.28) * mm});
            skLineSegment(sketch, "E15.13", {"start": v(24.8, -15.28) * mm, "end": v(21.87, -19.25) * mm});
            skLineSegment(sketch, "E15.14", {"start": v(21.87, -19.25) * mm, "end": v(18.3, -22.67) * mm});
            skLineSegment(sketch, "E15.15", {"start": v(18.3, -22.67) * mm, "end": v(14.2, -25.44) * mm});
            skLineSegment(sketch, "E15.16", {"start": v(14.2, -25.44) * mm, "end": v(9.7, -27.47) * mm});
            skLineSegment(sketch, "E15.17", {"start": v(9.7, -27.47) * mm, "end": v(4.92, -28.72) * mm});
            skLineSegment(sketch, "E15.18", {"start": v(4.92, -28.72) * mm, "end": v(0, -29.14) * mm});
            skLineSegment(sketch, "E15.19", {"start": v(0, -29.14) * mm, "end": v(-4.92, -28.72) * mm});
            skLineSegment(sketch, "E15.20", {"start": v(-4.92, -28.72) * mm, "end": v(-9.7, -27.47) * mm});
            skLineSegment(sketch, "E15.21", {"start": v(-9.7, -27.47) * mm, "end": v(-14.2, -25.44) * mm});
            skLineSegment(sketch, "E15.22", {"start": v(-14.2, -25.44) * mm, "end": v(-18.3, -22.67) * mm});
            skLineSegment(sketch, "E15.23", {"start": v(-18.3, -22.67) * mm, "end": v(-21.87, -19.25) * mm});
            skLineSegment(sketch, "E15.24", {"start": v(-21.87, -19.25) * mm, "end": v(-24.8, -15.28) * mm});
            skLineSegment(sketch, "E15.25", {"start": v(-24.8, -15.28) * mm, "end": v(-27.03, -10.86) * mm});
            skLineSegment(sketch, "E15.26", {"start": v(-27.03, -10.86) * mm, "end": v(-28.48, -6.14) * mm});
            skLineSegment(sketch, "E15.27", {"start": v(-28.48, -6.14) * mm, "end": v(-29.1, -1.24) * mm});
            skLineSegment(sketch, "E15.28", {"start": v(-29.1, -1.24) * mm, "end": v(-28.9, 3.7) * mm});
            skLineSegment(sketch, "E15.29", {"start": v(-28.9, 3.7) * mm, "end": v(-27.86, 8.53) * mm});
            skLineSegment(sketch, "E15.30", {"start": v(-27.86, 8.53) * mm, "end": v(-26.02, 13.12) * mm});
            skLineSegment(sketch, "E15.31", {"start": v(-26.02, 13.12) * mm, "end": v(-23.42, 17.32) * mm});
            skLineSegment(sketch, "E15.32", {"start": v(-23.42, 17.32) * mm, "end": v(-20.16, 21.03) * mm});
            skLineSegment(sketch, "E15.33", {"start": v(-20.16, 21.03) * mm, "end": v(-16.31, 24.14) * mm});
            skLineSegment(sketch, "E15.34", {"start": v(-16.31, 24.14) * mm, "end": v(-12, 26.55) * mm});
            skLineSegment(sketch, "E15.35", {"start": v(-12, 26.55) * mm, "end": v(-7.34, 28.2) * mm});
            skLineSegment(sketch, "E15.36", {"start": v(-7.34, 28.2) * mm, "end": v(-2.47, 29.03) * mm});
            skPoint(sketch, "E15.0.midPoint", {"position": v(0, 29.03) * mm});
            skSolve(sketch);
        }
        {
            var Q1;
            Q1=makeQuery(id+"F39.opLoft","CAP_FACE",FACE,{"disambiguationData":[OSD([makeQuery(id+"F38.imprint","IMPRINT",FACE,{"disambiguationData":[TD([[makeQuery(id+"F38.imprint","IMPRINT",EDGE,{"derivedFrom":sQuery(id+"F38.wireOp",EDGE,"E14.0")}),-1.0]])]})])],"isStart":true});
            var Q2;
            Q2=makeQuery(id+"F41.imprint","IMPRINT",FACE,{"disambiguationData":[TD([[makeQuery(id+"F41.imprint","IMPRINT",EDGE,{"derivedFrom":sQuery(id+"F41.wireOp",EDGE,"E15.0")}),-1.0]])]});
            loft(context, id + "F42", {"operationType" : NewBodyOperationType.ADD, "sheetProfilesArray" : [{ "sheetProfileEntities" : qUnion([Q1]) }, { "sheetProfileEntities" : qUnion([Q2]) }]});
        }
        {
            var Q0;
            Q0=qCreatedBy(id+"F40.planeOp",FACE);
            cPlane(context, id + "F43", {"entities" : qUnion([Q0]), "cplaneType" : CPlaneType.OFFSET, "offset" : 2.54 * mm, "width" : 152.4 * mm, "height" : 152.4 * mm});
        }
        {
            var Q0;
            Q0=qCreatedBy(id+"F43.planeOp",FACE);
            var sketch = newSketch(context, id + "F44", { "sketchPlane" : qUnion([Q0])});
            skCircle(sketch, "E16.cCircle", {"center": v(0, 0) * mm, "radius": 30.59 * mm, "construction": true});
            skLineSegment(sketch, "E16.0", {"start": v(-2.68, 30.59) * mm, "end": v(2.68, 30.59) * mm});
            skLineSegment(sketch, "E16.1", {"start": v(2.68, 30.59) * mm, "end": v(7.95, 29.66) * mm});
            skLineSegment(sketch, "E16.2", {"start": v(7.95, 29.66) * mm, "end": v(12.98, 27.83) * mm});
            skLineSegment(sketch, "E16.3", {"start": v(12.98, 27.83) * mm, "end": v(17.61, 25.15) * mm});
            skLineSegment(sketch, "E16.4", {"start": v(17.61, 25.15) * mm, "end": v(21.71, 21.71) * mm});
            skLineSegment(sketch, "E16.5", {"start": v(21.71, 21.71) * mm, "end": v(25.15, 17.61) * mm});
            skLineSegment(sketch, "E16.6", {"start": v(25.15, 17.61) * mm, "end": v(27.83, 12.98) * mm});
            skLineSegment(sketch, "E16.7", {"start": v(27.83, 12.98) * mm, "end": v(29.66, 7.95) * mm});
            skLineSegment(sketch, "E16.8", {"start": v(29.66, 7.95) * mm, "end": v(30.59, 2.68) * mm});
            skLineSegment(sketch, "E16.9", {"start": v(30.59, 2.68) * mm, "end": v(30.59, -2.68) * mm});
            skLineSegment(sketch, "E16.10", {"start": v(30.59, -2.68) * mm, "end": v(29.66, -7.95) * mm});
            skLineSegment(sketch, "E16.11", {"start": v(29.66, -7.95) * mm, "end": v(27.83, -12.98) * mm});
            skLineSegment(sketch, "E16.12", {"start": v(27.83, -12.98) * mm, "end": v(25.15, -17.61) * mm});
            skLineSegment(sketch, "E16.13", {"start": v(25.15, -17.61) * mm, "end": v(21.71, -21.71) * mm});
            skLineSegment(sketch, "E16.14", {"start": v(21.71, -21.71) * mm, "end": v(17.61, -25.15) * mm});
            skLineSegment(sketch, "E16.15", {"start": v(17.61, -25.15) * mm, "end": v(12.98, -27.83) * mm});
            skLineSegment(sketch, "E16.16", {"start": v(12.98, -27.83) * mm, "end": v(7.95, -29.66) * mm});
            skLineSegment(sketch, "E16.17", {"start": v(7.95, -29.66) * mm, "end": v(2.68, -30.59) * mm});
            skLineSegment(sketch, "E16.18", {"start": v(2.68, -30.59) * mm, "end": v(-2.68, -30.59) * mm});
            skLineSegment(sketch, "E16.19", {"start": v(-2.68, -30.59) * mm, "end": v(-7.95, -29.66) * mm});
            skLineSegment(sketch, "E16.20", {"start": v(-7.95, -29.66) * mm, "end": v(-12.98, -27.83) * mm});
            skLineSegment(sketch, "E16.21", {"start": v(-12.98, -27.83) * mm, "end": v(-17.61, -25.15) * mm});
            skLineSegment(sketch, "E16.22", {"start": v(-17.61, -25.15) * mm, "end": v(-21.71, -21.71) * mm});
            skLineSegment(sketch, "E16.23", {"start": v(-21.71, -21.71) * mm, "end": v(-25.15, -17.61) * mm});
            skLineSegment(sketch, "E16.24", {"start": v(-25.15, -17.61) * mm, "end": v(-27.83, -12.98) * mm});
            skLineSegment(sketch, "E16.25", {"start": v(-27.83, -12.98) * mm, "end": v(-29.66, -7.95) * mm});
            skLineSegment(sketch, "E16.26", {"start": v(-29.66, -7.95) * mm, "end": v(-30.59, -2.68) * mm});
            skLineSegment(sketch, "E16.27", {"start": v(-30.59, -2.68) * mm, "end": v(-30.59, 2.68) * mm});
            skLineSegment(sketch, "E16.28", {"start": v(-30.59, 2.68) * mm, "end": v(-29.66, 7.95) * mm});
            skLineSegment(sketch, "E16.29", {"start": v(-29.66, 7.95) * mm, "end": v(-27.83, 12.98) * mm});
            skLineSegment(sketch, "E16.30", {"start": v(-27.83, 12.98) * mm, "end": v(-25.15, 17.61) * mm});
            skLineSegment(sketch, "E16.31", {"start": v(-25.15, 17.61) * mm, "end": v(-21.71, 21.71) * mm});
            skLineSegment(sketch, "E16.32", {"start": v(-21.71, 21.71) * mm, "end": v(-17.61, 25.15) * mm});
            skLineSegment(sketch, "E16.33", {"start": v(-17.61, 25.15) * mm, "end": v(-12.98, 27.83) * mm});
            skLineSegment(sketch, "E16.34", {"start": v(-12.98, 27.83) * mm, "end": v(-7.95, 29.66) * mm});
            skLineSegment(sketch, "E16.35", {"start": v(-7.95, 29.66) * mm, "end": v(-2.68, 30.59) * mm});
            skPoint(sketch, "E16.0.midPoint", {"position": v(0, 30.59) * mm});
            skSolve(sketch);
        }
        {
            var Q1;
            Q1=makeQuery(id+"F42.opLoft","CAP_FACE",FACE,{"disambiguationData":[OSD([makeQuery(id+"F41.imprint","IMPRINT",FACE,{"disambiguationData":[TD([[makeQuery(id+"F41.imprint","IMPRINT",EDGE,{"derivedFrom":sQuery(id+"F41.wireOp",EDGE,"E15.0")}),-1.0]])]})])],"isStart":true});
            var Q2;
            Q2=makeQuery(id+"F44.imprint","IMPRINT",FACE,{"disambiguationData":[TD([[makeQuery(id+"F44.imprint","IMPRINT",EDGE,{"derivedFrom":sQuery(id+"F44.wireOp",EDGE,"E16.0")}),-1.0]])]});
            loft(context, id + "F45", {"operationType" : NewBodyOperationType.ADD, "sheetProfilesArray" : [{ "sheetProfileEntities" : qUnion([Q1]) }, { "sheetProfileEntities" : qUnion([Q2]) }]});
        }
        {
            var Q0;
            Q0=qCreatedBy(id+"F43.planeOp",FACE);
            cPlane(context, id + "F46", {"entities" : qUnion([Q0]), "cplaneType" : CPlaneType.OFFSET, "offset" : 2.54 * mm, "width" : 152.4 * mm, "height" : 152.4 * mm});
        }
        {
            var Q0;
            Q0=qCreatedBy(id+"F46.planeOp",FACE);
            var sketch = newSketch(context, id + "F47", { "sketchPlane" : qUnion([Q0])});
            skCircle(sketch, "E17.cCircle", {"center": v(0, 0) * mm, "radius": 31.72 * mm, "construction": true});
            skLineSegment(sketch, "E17.0", {"start": v(-2.78, 31.72) * mm, "end": v(2.78, 31.72) * mm});
            skLineSegment(sketch, "E17.1", {"start": v(2.78, 31.72) * mm, "end": v(8.24, 30.76) * mm});
            skLineSegment(sketch, "E17.2", {"start": v(8.24, 30.76) * mm, "end": v(13.46, 28.86) * mm});
            skLineSegment(sketch, "E17.3", {"start": v(13.46, 28.86) * mm, "end": v(18.26, 26.08) * mm});
            skLineSegment(sketch, "E17.4", {"start": v(18.26, 26.08) * mm, "end": v(22.52, 22.52) * mm});
            skLineSegment(sketch, "E17.5", {"start": v(22.52, 22.52) * mm, "end": v(26.08, 18.26) * mm});
            skLineSegment(sketch, "E17.6", {"start": v(26.08, 18.26) * mm, "end": v(28.86, 13.46) * mm});
            skLineSegment(sketch, "E17.7", {"start": v(28.86, 13.46) * mm, "end": v(30.76, 8.24) * mm});
            skLineSegment(sketch, "E17.8", {"start": v(30.76, 8.24) * mm, "end": v(31.72, 2.78) * mm});
            skLineSegment(sketch, "E17.9", {"start": v(31.72, 2.78) * mm, "end": v(31.72, -2.78) * mm});
            skLineSegment(sketch, "E17.10", {"start": v(31.72, -2.78) * mm, "end": v(30.76, -8.24) * mm});
            skLineSegment(sketch, "E17.11", {"start": v(30.76, -8.24) * mm, "end": v(28.86, -13.46) * mm});
            skLineSegment(sketch, "E17.12", {"start": v(28.86, -13.46) * mm, "end": v(26.08, -18.26) * mm});
            skLineSegment(sketch, "E17.13", {"start": v(26.08, -18.26) * mm, "end": v(22.52, -22.52) * mm});
            skLineSegment(sketch, "E17.14", {"start": v(22.52, -22.52) * mm, "end": v(18.26, -26.08) * mm});
            skLineSegment(sketch, "E17.15", {"start": v(18.26, -26.08) * mm, "end": v(13.46, -28.86) * mm});
            skLineSegment(sketch, "E17.16", {"start": v(13.46, -28.86) * mm, "end": v(8.24, -30.76) * mm});
            skLineSegment(sketch, "E17.17", {"start": v(8.24, -30.76) * mm, "end": v(2.78, -31.72) * mm});
            skLineSegment(sketch, "E17.18", {"start": v(2.78, -31.72) * mm, "end": v(-2.78, -31.72) * mm});
            skLineSegment(sketch, "E17.19", {"start": v(-2.78, -31.72) * mm, "end": v(-8.24, -30.76) * mm});
            skLineSegment(sketch, "E17.20", {"start": v(-8.24, -30.76) * mm, "end": v(-13.46, -28.86) * mm});
            skLineSegment(sketch, "E17.21", {"start": v(-13.46, -28.86) * mm, "end": v(-18.26, -26.08) * mm});
            skLineSegment(sketch, "E17.22", {"start": v(-18.26, -26.08) * mm, "end": v(-22.52, -22.52) * mm});
            skLineSegment(sketch, "E17.23", {"start": v(-22.52, -22.52) * mm, "end": v(-26.08, -18.26) * mm});
            skLineSegment(sketch, "E17.24", {"start": v(-26.08, -18.26) * mm, "end": v(-28.86, -13.46) * mm});
            skLineSegment(sketch, "E17.25", {"start": v(-28.86, -13.46) * mm, "end": v(-30.76, -8.24) * mm});
            skLineSegment(sketch, "E17.26", {"start": v(-30.76, -8.24) * mm, "end": v(-31.72, -2.78) * mm});
            skLineSegment(sketch, "E17.27", {"start": v(-31.72, -2.78) * mm, "end": v(-31.72, 2.78) * mm});
            skLineSegment(sketch, "E17.28", {"start": v(-31.72, 2.78) * mm, "end": v(-30.76, 8.24) * mm});
            skLineSegment(sketch, "E17.29", {"start": v(-30.76, 8.24) * mm, "end": v(-28.86, 13.46) * mm});
            skLineSegment(sketch, "E17.30", {"start": v(-28.86, 13.46) * mm, "end": v(-26.08, 18.26) * mm});
            skLineSegment(sketch, "E17.31", {"start": v(-26.08, 18.26) * mm, "end": v(-22.52, 22.52) * mm});
            skLineSegment(sketch, "E17.32", {"start": v(-22.52, 22.52) * mm, "end": v(-18.26, 26.08) * mm});
            skLineSegment(sketch, "E17.33", {"start": v(-18.26, 26.08) * mm, "end": v(-13.46, 28.86) * mm});
            skLineSegment(sketch, "E17.34", {"start": v(-13.46, 28.86) * mm, "end": v(-8.24, 30.76) * mm});
            skLineSegment(sketch, "E17.35", {"start": v(-8.24, 30.76) * mm, "end": v(-2.78, 31.72) * mm});
            skPoint(sketch, "E17.0.midPoint", {"position": v(0, 31.72) * mm});
            skSolve(sketch);
        }
        {
            var Q1;
            Q1=makeQuery(id+"F45.opLoft","CAP_FACE",FACE,{"disambiguationData":[OSD([makeQuery(id+"F44.imprint","IMPRINT",FACE,{"disambiguationData":[TD([[makeQuery(id+"F44.imprint","IMPRINT",EDGE,{"derivedFrom":sQuery(id+"F44.wireOp",EDGE,"E16.0")}),-1.0]])]})])],"isStart":true});
            var Q2;
            Q2=makeQuery(id+"F47.imprint","IMPRINT",FACE,{"disambiguationData":[TD([[makeQuery(id+"F47.imprint","IMPRINT",EDGE,{"derivedFrom":sQuery(id+"F47.wireOp",EDGE,"E17.0")}),-1.0]])]});
            loft(context, id + "F48", {"operationType" : NewBodyOperationType.ADD, "sheetProfilesArray" : [{ "sheetProfileEntities" : qUnion([Q1]) }, { "sheetProfileEntities" : qUnion([Q2]) }]});
        }
        {
            var Q0;
            Q0=qCreatedBy(id+"F46.planeOp",FACE);
            cPlane(context, id + "F49", {"entities" : qUnion([Q0]), "cplaneType" : CPlaneType.OFFSET, "offset" : 2.54 * mm, "width" : 152.4 * mm, "height" : 152.4 * mm});
        }
        {
            var Q0;
            Q0=qCreatedBy(id+"F49.planeOp",FACE);
            var sketch = newSketch(context, id + "F50", { "sketchPlane" : qUnion([Q0])});
            skCircle(sketch, "E18.cCircle", {"center": v(0, 0) * mm, "radius": 33.14 * mm, "construction": true});
            skLineSegment(sketch, "E18.0", {"start": v(-2.98, 33.14) * mm, "end": v(2.98, 33.14) * mm});
            skLineSegment(sketch, "E18.1", {"start": v(2.98, 33.14) * mm, "end": v(8.85, 32.07) * mm});
            skLineSegment(sketch, "E18.2", {"start": v(8.85, 32.07) * mm, "end": v(14.44, 29.98) * mm});
            skLineSegment(sketch, "E18.3", {"start": v(14.44, 29.98) * mm, "end": v(19.56, 26.92) * mm});
            skLineSegment(sketch, "E18.4", {"start": v(19.56, 26.92) * mm, "end": v(24.05, 23) * mm});
            skLineSegment(sketch, "E18.5", {"start": v(24.05, 23) * mm, "end": v(27.77, 18.33) * mm});
            skLineSegment(sketch, "E18.6", {"start": v(27.77, 18.33) * mm, "end": v(30.6, 13.08) * mm});
            skLineSegment(sketch, "E18.7", {"start": v(30.6, 13.08) * mm, "end": v(32.44, 7.4) * mm});
            skLineSegment(sketch, "E18.8", {"start": v(32.44, 7.4) * mm, "end": v(33.24, 1.5) * mm});
            skLineSegment(sketch, "E18.9", {"start": v(33.24, 1.5) * mm, "end": v(32.97, -4.47) * mm});
            skLineSegment(sketch, "E18.10", {"start": v(32.97, -4.47) * mm, "end": v(31.64, -10.28) * mm});
            skLineSegment(sketch, "E18.11", {"start": v(31.64, -10.28) * mm, "end": v(29.3, -15.77) * mm});
            skLineSegment(sketch, "E18.12", {"start": v(29.3, -15.77) * mm, "end": v(26.01, -20.74) * mm});
            skLineSegment(sketch, "E18.13", {"start": v(26.01, -20.74) * mm, "end": v(21.9, -25.06) * mm});
            skLineSegment(sketch, "E18.14", {"start": v(21.9, -25.06) * mm, "end": v(17.06, -28.56) * mm});
            skLineSegment(sketch, "E18.15", {"start": v(17.06, -28.56) * mm, "end": v(11.7, -31.15) * mm});
            skLineSegment(sketch, "E18.16", {"start": v(11.7, -31.15) * mm, "end": v(5.94, -32.74) * mm});
            skLineSegment(sketch, "E18.17", {"start": v(5.94, -32.74) * mm, "end": v(0, -33.27) * mm});
            skLineSegment(sketch, "E18.18", {"start": v(0, -33.27) * mm, "end": v(-5.94, -32.74) * mm});
            skLineSegment(sketch, "E18.19", {"start": v(-5.94, -32.74) * mm, "end": v(-11.7, -31.15) * mm});
            skLineSegment(sketch, "E18.20", {"start": v(-11.7, -31.15) * mm, "end": v(-17.06, -28.56) * mm});
            skLineSegment(sketch, "E18.21", {"start": v(-17.06, -28.56) * mm, "end": v(-21.9, -25.06) * mm});
            skLineSegment(sketch, "E18.22", {"start": v(-21.9, -25.06) * mm, "end": v(-26.01, -20.74) * mm});
            skLineSegment(sketch, "E18.23", {"start": v(-26.01, -20.74) * mm, "end": v(-29.3, -15.77) * mm});
            skLineSegment(sketch, "E18.24", {"start": v(-29.3, -15.77) * mm, "end": v(-31.64, -10.28) * mm});
            skLineSegment(sketch, "E18.25", {"start": v(-31.64, -10.28) * mm, "end": v(-32.97, -4.47) * mm});
            skLineSegment(sketch, "E18.26", {"start": v(-32.97, -4.47) * mm, "end": v(-33.24, 1.5) * mm});
            skLineSegment(sketch, "E18.27", {"start": v(-33.24, 1.5) * mm, "end": v(-32.44, 7.4) * mm});
            skLineSegment(sketch, "E18.28", {"start": v(-32.44, 7.4) * mm, "end": v(-30.6, 13.08) * mm});
            skLineSegment(sketch, "E18.29", {"start": v(-30.6, 13.08) * mm, "end": v(-27.77, 18.33) * mm});
            skLineSegment(sketch, "E18.30", {"start": v(-27.77, 18.33) * mm, "end": v(-24.05, 23) * mm});
            skLineSegment(sketch, "E18.31", {"start": v(-24.05, 23) * mm, "end": v(-19.56, 26.92) * mm});
            skLineSegment(sketch, "E18.32", {"start": v(-19.56, 26.92) * mm, "end": v(-14.44, 29.98) * mm});
            skLineSegment(sketch, "E18.33", {"start": v(-14.44, 29.98) * mm, "end": v(-8.85, 32.07) * mm});
            skLineSegment(sketch, "E18.34", {"start": v(-8.85, 32.07) * mm, "end": v(-2.98, 33.14) * mm});
            skPoint(sketch, "E18.0.midPoint", {"position": v(0, 33.14) * mm});
            skSolve(sketch);
        }
        {
            var Q1;
            Q1=makeQuery(id+"F48.opLoft","CAP_FACE",FACE,{"disambiguationData":[OSD([makeQuery(id+"F47.imprint","IMPRINT",FACE,{"disambiguationData":[TD([[makeQuery(id+"F47.imprint","IMPRINT",EDGE,{"derivedFrom":sQuery(id+"F47.wireOp",EDGE,"E17.0")}),-1.0]])]})])],"isStart":true});
            var Q2;
            Q2=makeQuery(id+"F50.imprint","IMPRINT",FACE,{"disambiguationData":[TD([[makeQuery(id+"F50.imprint","IMPRINT",EDGE,{"derivedFrom":sQuery(id+"F50.wireOp",EDGE,"E18.0")}),-1.0]])]});
            loft(context, id + "F51", {"operationType" : NewBodyOperationType.ADD, "sheetProfilesArray" : [{ "sheetProfileEntities" : qUnion([Q1]) }, { "sheetProfileEntities" : qUnion([Q2]) }]});
        }
        {
            var Q0;
            Q0=qCreatedBy(id+"F49.planeOp",FACE);
            cPlane(context, id + "F52", {"entities" : qUnion([Q0]), "cplaneType" : CPlaneType.OFFSET, "offset" : 2.54 * mm, "width" : 152.4 * mm, "height" : 152.4 * mm});
        }
        {
            var Q0;
            Q0=qCreatedBy(id+"F52.planeOp",FACE);
            var sketch = newSketch(context, id + "F53", { "sketchPlane" : qUnion([Q0])});
            skCircle(sketch, "E19.cCircle", {"center": v(0, 0) * mm, "radius": 34.41 * mm, "construction": true});
            skLineSegment(sketch, "E19.0", {"start": v(-3.1, 34.41) * mm, "end": v(3.1, 34.41) * mm});
            skLineSegment(sketch, "E19.1", {"start": v(3.1, 34.41) * mm, "end": v(9.2, 33.3) * mm});
            skLineSegment(sketch, "E19.2", {"start": v(9.2, 33.3) * mm, "end": v(15, 31.13) * mm});
            skLineSegment(sketch, "E19.3", {"start": v(15, 31.13) * mm, "end": v(20.3, 27.95) * mm});
            skLineSegment(sketch, "E19.4", {"start": v(20.3, 27.95) * mm, "end": v(24.97, 23.88) * mm});
            skLineSegment(sketch, "E19.5", {"start": v(24.97, 23.88) * mm, "end": v(28.83, 19.03) * mm});
            skLineSegment(sketch, "E19.6", {"start": v(28.83, 19.03) * mm, "end": v(31.77, 13.58) * mm});
            skLineSegment(sketch, "E19.7", {"start": v(31.77, 13.58) * mm, "end": v(33.68, 7.69) * mm});
            skLineSegment(sketch, "E19.8", {"start": v(33.68, 7.69) * mm, "end": v(34.52, 1.55) * mm});
            skLineSegment(sketch, "E19.9", {"start": v(34.52, 1.55) * mm, "end": v(34.24, -4.64) * mm});
            skLineSegment(sketch, "E19.10", {"start": v(34.24, -4.64) * mm, "end": v(32.86, -10.68) * mm});
            skLineSegment(sketch, "E19.11", {"start": v(32.86, -10.68) * mm, "end": v(30.42, -16.37) * mm});
            skLineSegment(sketch, "E19.12", {"start": v(30.42, -16.37) * mm, "end": v(27.01, -21.54) * mm});
            skLineSegment(sketch, "E19.13", {"start": v(27.01, -21.54) * mm, "end": v(22.73, -26.02) * mm});
            skLineSegment(sketch, "E19.14", {"start": v(22.73, -26.02) * mm, "end": v(17.72, -29.66) * mm});
            skLineSegment(sketch, "E19.15", {"start": v(17.72, -29.66) * mm, "end": v(12.14, -32.35) * mm});
            skLineSegment(sketch, "E19.16", {"start": v(12.14, -32.35) * mm, "end": v(6.17, -34) * mm});
            skLineSegment(sketch, "E19.17", {"start": v(6.17, -34) * mm, "end": v(0, -34.55) * mm});
            skLineSegment(sketch, "E19.18", {"start": v(0, -34.55) * mm, "end": v(-6.17, -34) * mm});
            skLineSegment(sketch, "E19.19", {"start": v(-6.17, -34) * mm, "end": v(-12.14, -32.35) * mm});
            skLineSegment(sketch, "E19.20", {"start": v(-12.14, -32.35) * mm, "end": v(-17.72, -29.66) * mm});
            skLineSegment(sketch, "E19.21", {"start": v(-17.72, -29.66) * mm, "end": v(-22.73, -26.02) * mm});
            skLineSegment(sketch, "E19.22", {"start": v(-22.73, -26.02) * mm, "end": v(-27.01, -21.54) * mm});
            skLineSegment(sketch, "E19.23", {"start": v(-27.01, -21.54) * mm, "end": v(-30.42, -16.37) * mm});
            skLineSegment(sketch, "E19.24", {"start": v(-30.42, -16.37) * mm, "end": v(-32.86, -10.68) * mm});
            skLineSegment(sketch, "E19.25", {"start": v(-32.86, -10.68) * mm, "end": v(-34.24, -4.64) * mm});
            skLineSegment(sketch, "E19.26", {"start": v(-34.24, -4.64) * mm, "end": v(-34.52, 1.55) * mm});
            skLineSegment(sketch, "E19.27", {"start": v(-34.52, 1.55) * mm, "end": v(-33.68, 7.69) * mm});
            skLineSegment(sketch, "E19.28", {"start": v(-33.68, 7.69) * mm, "end": v(-31.77, 13.58) * mm});
            skLineSegment(sketch, "E19.29", {"start": v(-31.77, 13.58) * mm, "end": v(-28.83, 19.03) * mm});
            skLineSegment(sketch, "E19.30", {"start": v(-28.83, 19.03) * mm, "end": v(-24.97, 23.88) * mm});
            skLineSegment(sketch, "E19.31", {"start": v(-24.97, 23.88) * mm, "end": v(-20.3, 27.95) * mm});
            skLineSegment(sketch, "E19.32", {"start": v(-20.3, 27.95) * mm, "end": v(-15, 31.13) * mm});
            skLineSegment(sketch, "E19.33", {"start": v(-15, 31.13) * mm, "end": v(-9.2, 33.3) * mm});
            skLineSegment(sketch, "E19.34", {"start": v(-9.2, 33.3) * mm, "end": v(-3.1, 34.41) * mm});
            skPoint(sketch, "E19.0.midPoint", {"position": v(0, 34.41) * mm});
            skSolve(sketch);
        }
        {
            var Q1;
            Q1=makeQuery(id+"F51.opLoft","CAP_FACE",FACE,{"disambiguationData":[OSD([makeQuery(id+"F50.imprint","IMPRINT",FACE,{"disambiguationData":[TD([[makeQuery(id+"F50.imprint","IMPRINT",EDGE,{"derivedFrom":sQuery(id+"F50.wireOp",EDGE,"E18.0")}),-1.0]])]})])],"isStart":true});
            var Q2;
            Q2=makeQuery(id+"F53.imprint","IMPRINT",FACE,{"disambiguationData":[TD([[makeQuery(id+"F53.imprint","IMPRINT",EDGE,{"derivedFrom":sQuery(id+"F53.wireOp",EDGE,"E19.0")}),-1.0]])]});
            loft(context, id + "F54", {"operationType" : NewBodyOperationType.ADD, "sheetProfilesArray" : [{ "sheetProfileEntities" : qUnion([Q1]) }, { "sheetProfileEntities" : qUnion([Q2]) }]});
        }
    });
